annotation { "Feature Type Name" : "Feature", "Feature Type Description" : "" }
export const myFeature = defineFeature(function(context is Context, id is Id, definition is map)
    precondition{}
    {
        {
            var Q0;
            Q0=qCreatedBy(makeId("Top.planeOp"),FACE);
            var sketch = newSketch(context, id + "F0", { "sketchPlane" : qUnion([Q0])});
            skPoint(sketch, "E0.0", {"position": v(5.76, 3.36) * mm});
            skPoint(sketch, "E1.0", {"position": v(6.94, 3.46) * mm});
            skPoint(sketch, "E2.0", {"position": v(8.14, 3.52) * mm});
            skPoint(sketch, "E3.0", {"position": v(9.34, 3.55) * mm});
            skPoint(sketch, "E4.0", {"position": v(10.55, 3.56) * mm});
            skPoint(sketch, "E5.0", {"position": v(11.74, 3.54) * mm});
            skPoint(sketch, "E6.0", {"position": v(12.92, 3.51) * mm});
            skPoint(sketch, "E7.0", {"position": v(14.07, 3.48) * mm});
            skPoint(sketch, "E8.0", {"position": v(15.2, 3.46) * mm});
            skPoint(sketch, "E9.0", {"position": v(16.27, 3.44) * mm});
            skPoint(sketch, "E10.0", {"position": v(17.17, 3.43) * mm});
            skPoint(sketch, "E11.0", {"position": v(17.88, 3.43) * mm});
            skPoint(sketch, "E12.0", {"position": v(18.44, 3.43) * mm});
            skPoint(sketch, "E13.0", {"position": v(18.9, 3.43) * mm});
            skPoint(sketch, "E14.0", {"position": v(19.8, 3.43) * mm});
            skPoint(sketch, "E15.0", {"position": v(20.34, 3.43) * mm});
            skPoint(sketch, "E16.0", {"position": v(21, 3.42) * mm});
            skPoint(sketch, "E17.0", {"position": v(21.87, 3.4) * mm});
            skPoint(sketch, "E18.0", {"position": v(22.97, 3.37) * mm});
            skPoint(sketch, "E19.0", {"position": v(24.38, 3.33) * mm});
            skPoint(sketch, "E20.0", {"position": v(26.14, 3.27) * mm});
            skPoint(sketch, "E21.0", {"position": v(26.51, 3.2) * mm});
            skPoint(sketch, "E22.0", {"position": v(26.85, 3) * mm});
            skPoint(sketch, "E23.0", {"position": v(27.16, 2.72) * mm});
            skPoint(sketch, "E24.0", {"position": v(27.44, 2.35) * mm});
            skPoint(sketch, "E25.0", {"position": v(27.69, 1.92) * mm});
            skPoint(sketch, "E26.0", {"position": v(27.92, 1.45) * mm});
            skPoint(sketch, "E27.0", {"position": v(28.12, 0.94) * mm});
            skPoint(sketch, "E28.0", {"position": v(28.3, 0.43) * mm});
            skPoint(sketch, "E29.0", {"position": v(28.47, -0.07) * mm});
            skPoint(sketch, "E30.0", {"position": v(28.62, -0.55) * mm});
            skPoint(sketch, "E31.0", {"position": v(28.76, -1) * mm});
            skPoint(sketch, "E32.0", {"position": v(28.88, -1.37) * mm});
            skPoint(sketch, "E33.0", {"position": v(29.06, -1.72) * mm});
            skPoint(sketch, "E34.0", {"position": v(29.3, -2) * mm});
            skPoint(sketch, "E35.0", {"position": v(29.58, -2.16) * mm});
            skPoint(sketch, "E36.0", {"position": v(29.9, -2.22) * mm});
            skPoint(sketch, "E37.0", {"position": v(30.26, -2.13) * mm});
            skPoint(sketch, "E38.0", {"position": v(30.62, -1.89) * mm});
            skPoint(sketch, "E39.0", {"position": v(30.98, -1.47) * mm});
            skPoint(sketch, "E40.0", {"position": v(31.33, -0.85) * mm});
            skPoint(sketch, "E41.0", {"position": v(31.66, -0.02) * mm});
            skPoint(sketch, "E42.0", {"position": v(31.94, 1.04) * mm});
            skPoint(sketch, "E43.0", {"position": v(32.17, 2.36) * mm});
            skPoint(sketch, "E44.0", {"position": v(32.34, 3.95) * mm});
            skPoint(sketch, "E45.0", {"position": v(31.94, 5.71) * mm});
            skPoint(sketch, "E46.0", {"position": v(30.52, 7.1) * mm});
            skPoint(sketch, "E47.0", {"position": v(28.22, 8.13) * mm});
            skPoint(sketch, "E48.0", {"position": v(25.18, 8.86) * mm});
            skPoint(sketch, "E49.0", {"position": v(21.51, 9.33) * mm});
            skPoint(sketch, "E50.0", {"position": v(17.37, 9.58) * mm});
            skPoint(sketch, "E51.0", {"position": v(12.88, 9.65) * mm});
            skPoint(sketch, "E52.0", {"position": v(8.18, 9.59) * mm});
            skPoint(sketch, "E53.0", {"position": v(3.4, 9.42) * mm});
            skPoint(sketch, "E54.0", {"position": v(-14.33, 8.55) * mm});
            skPoint(sketch, "E55.0", {"position": v(-10.12, 8.78) * mm});
            skPoint(sketch, "E56.0", {"position": v(-5.9, 8.98) * mm});
            skPoint(sketch, "E57.0", {"position": v(-1.34, 9.2) * mm});
            skPoint(sketch, "E58.0", {"position": v(-19.1, 8.2) * mm});
            skPoint(sketch, "E59.0", {"position": v(-24.25, 7.73) * mm});
            skPoint(sketch, "E60.0", {"position": v(-29.6, 7.16) * mm});
            skPoint(sketch, "E61.0", {"position": v(-35, 6.5) * mm});
            skPoint(sketch, "E62.0", {"position": v(-40.24, 5.75) * mm});
            skPoint(sketch, "E63.0", {"position": v(-45.17, 4.92) * mm});
            skPoint(sketch, "E64.0", {"position": v(-49.6, 4.03) * mm});
            skPoint(sketch, "E65.0", {"position": v(-53.38, 3.07) * mm});
            skPoint(sketch, "E66.0", {"position": v(-56.31, 2.08) * mm});
            skPoint(sketch, "E67.0", {"position": v(-58.23, 1.04) * mm});
            skPoint(sketch, "E68.0", {"position": v(-58.96, -0.03) * mm});
            skPoint(sketch, "E69.0", {"position": v(-58.54, -1.04) * mm});
            skPoint(sketch, "E70.0", {"position": v(-57.22, -1.7) * mm});
            skPoint(sketch, "E71.0", {"position": v(-55.14, -2.02) * mm});
            skPoint(sketch, "E72.0", {"position": v(-49.2, -1.91) * mm});
            skPoint(sketch, "E73.0", {"position": v(-45.64, -1.57) * mm});
            skPoint(sketch, "E74.0", {"position": v(-41.85, -1.1) * mm});
            skPoint(sketch, "E75.0", {"position": v(-37.98, -0.57) * mm});
            skPoint(sketch, "E76.0", {"position": v(-34.17, 0) * mm});
            skPoint(sketch, "E77.0", {"position": v(-30.54, 0.55) * mm});
            skPoint(sketch, "E78.0", {"position": v(-27.24, 1.03) * mm});
            skPoint(sketch, "E79.0", {"position": v(-24.4, 1.4) * mm});
            skPoint(sketch, "E80.0", {"position": v(-20.27, 1.18) * mm});
            skPoint(sketch, "E81.0", {"position": v(-18.42, 0.62) * mm});
            skPoint(sketch, "E82.0", {"position": v(-16.71, -0.18) * mm});
            skPoint(sketch, "E83.0", {"position": v(-15.15, -1.14) * mm});
            skPoint(sketch, "E84.0", {"position": v(-22.27, 1.45) * mm});
            skPoint(sketch, "E85.0", {"position": v(-13.73, -2.24) * mm});
            skPoint(sketch, "E86.0", {"position": v(-12.46, -3.4) * mm});
            skPoint(sketch, "E87.0", {"position": v(-11.33, -4.59) * mm});
            skPoint(sketch, "E88.0", {"position": v(-10.34, -5.74) * mm});
            skPoint(sketch, "E89.0", {"position": v(-9.5, -6.8) * mm});
            skPoint(sketch, "E90.0", {"position": v(-8.8, -7.72) * mm});
            skPoint(sketch, "E91.0", {"position": v(-8.24, -8.44) * mm});
            skPoint(sketch, "E92.0", {"position": v(-8.78, -8.36) * mm});
            skPoint(sketch, "E93.0", {"position": v(-7.6, -9.13) * mm});
            skPoint(sketch, "E94.0", {"position": v(-6.87, -9.74) * mm});
            skPoint(sketch, "E95.0", {"position": v(-5.2, -10.7) * mm});
            skPoint(sketch, "E96.0", {"position": v(-6.06, -10.27) * mm});
            skPoint(sketch, "E97.0", {"position": v(-4.32, -11.02) * mm});
            skPoint(sketch, "E98.0", {"position": v(-3.44, -11.23) * mm});
            skPoint(sketch, "E99.0", {"position": v(-2.59, -11.32) * mm});
            skPoint(sketch, "E100.0", {"position": v(-1.8, -11.27) * mm});
            skPoint(sketch, "E101.0", {"position": v(-1.08, -11.09) * mm});
            skPoint(sketch, "E102.0", {"position": v(-0.47, -10.75) * mm});
            skPoint(sketch, "E103.0", {"position": v(0, -10.24) * mm});
            skPoint(sketch, "E104.0", {"position": v(0.31, -9.57) * mm});
            skPoint(sketch, "E105.0", {"position": v(0.6, -8.64) * mm});
            skPoint(sketch, "E106.0", {"position": v(0.9, -7.79) * mm});
            skPoint(sketch, "E107.0", {"position": v(1.18, -7) * mm});
            skPoint(sketch, "E108.0", {"position": v(1.44, -6.3) * mm});
            skPoint(sketch, "E109.0", {"position": v(1.67, -5.7) * mm});
            skPoint(sketch, "E110.0", {"position": v(1.84, -5.19) * mm});
            skPoint(sketch, "E111.0", {"position": v(1.95, -4.78) * mm});
            skPoint(sketch, "E112.0", {"position": v(1.98, -4.48) * mm});
            skPoint(sketch, "E113.0", {"position": v(1.92, -4.3) * mm});
            skPoint(sketch, "E114.0", {"position": v(1.48, -4.32) * mm});
            skPoint(sketch, "E115.0", {"position": v(1.08, -4.54) * mm});
            skPoint(sketch, "E116.0", {"position": v(0.17, -4.94) * mm});
            skPoint(sketch, "E117.0", {"position": v(-0.46, -4.93) * mm});
            skPoint(sketch, "E118.0", {"position": v(-0.84, -4.57) * mm});
            skPoint(sketch, "E119.0", {"position": v(-1, -3.93) * mm});
            skPoint(sketch, "E120.0", {"position": v(-0.98, -3.08) * mm});
            skPoint(sketch, "E121.0", {"position": v(-0.78, -2.1) * mm});
            skPoint(sketch, "E122.0", {"position": v(-0.45, -1.05) * mm});
            skPoint(sketch, "E123.0", {"position": v(0, 0) * mm});
            skPoint(sketch, "E124.0", {"position": v(0.54, 0.98) * mm});
            skPoint(sketch, "E125.0", {"position": v(1.13, 1.8) * mm});
            skPoint(sketch, "E126.0", {"position": v(1.76, 2.43) * mm});
            skPoint(sketch, "E127.0", {"position": v(2.4, 2.77) * mm});
            skPoint(sketch, "E128.0", {"position": v(3.48, 3.02) * mm});
            skPoint(sketch, "E129.0", {"position": v(4.6, 3.22) * mm});
            skLineSegment(sketch, "E130", {"start": v(-56.31, 2.08) * mm, "end": v(-53.38, 3.07) * mm});
            skLineSegment(sketch, "E131", {"start": v(-49.6, 4.03) * mm, "end": v(-53.38, 3.07) * mm});
            skLineSegment(sketch, "E132", {"start": v(-49.6, 4.03) * mm, "end": v(-45.17, 4.92) * mm});
            skLineSegment(sketch, "E133", {"start": v(-45.17, 4.92) * mm, "end": v(-40.24, 5.75) * mm});
            skLineSegment(sketch, "E134", {"start": v(-40.24, 5.75) * mm, "end": v(-35, 6.5) * mm});
            skLineSegment(sketch, "E135", {"start": v(-35, 6.5) * mm, "end": v(-29.6, 7.16) * mm});
            skLineSegment(sketch, "E136", {"start": v(-29.6, 7.16) * mm, "end": v(-24.25, 7.73) * mm});
            skLineSegment(sketch, "E137", {"start": v(-24.25, 7.73) * mm, "end": v(-19.1, 8.2) * mm});
            skLineSegment(sketch, "E138", {"start": v(-19.1, 8.2) * mm, "end": v(-14.33, 8.55) * mm});
            skLineSegment(sketch, "E139", {"start": v(-14.33, 8.55) * mm, "end": v(-10.12, 8.78) * mm});
            skLineSegment(sketch, "E140", {"start": v(-10.12, 8.78) * mm, "end": v(-5.9, 8.98) * mm});
            skLineSegment(sketch, "E141", {"start": v(-5.9, 8.98) * mm, "end": v(-1.34, 9.2) * mm});
            skLineSegment(sketch, "E142", {"start": v(-1.34, 9.2) * mm, "end": v(3.4, 9.42) * mm});
            skLineSegment(sketch, "E143", {"start": v(3.4, 9.42) * mm, "end": v(8.18, 9.59) * mm});
            skLineSegment(sketch, "E144", {"start": v(8.18, 9.59) * mm, "end": v(12.88, 9.65) * mm});
            skLineSegment(sketch, "E145", {"start": v(12.88, 9.65) * mm, "end": v(17.37, 9.58) * mm});
            skLineSegment(sketch, "E146", {"start": v(17.37, 9.58) * mm, "end": v(21.51, 9.33) * mm});
            skLineSegment(sketch, "E147", {"start": v(21.51, 9.33) * mm, "end": v(25.18, 8.86) * mm});
            skLineSegment(sketch, "E148", {"start": v(28.22, 8.13) * mm, "end": v(25.18, 8.86) * mm});
            skLineSegment(sketch, "E149", {"start": v(28.22, 8.13) * mm, "end": v(30.52, 7.1) * mm});
            skLineSegment(sketch, "E150", {"start": v(30.52, 7.1) * mm, "end": v(31.94, 5.71) * mm});
            skLineSegment(sketch, "E151", {"start": v(31.94, 5.71) * mm, "end": v(32.34, 3.95) * mm});
            skLineSegment(sketch, "E152", {"start": v(32.34, 3.95) * mm, "end": v(32.17, 2.36) * mm});
            skLineSegment(sketch, "E153", {"start": v(32.17, 2.36) * mm, "end": v(31.94, 1.04) * mm});
            skLineSegment(sketch, "E154", {"start": v(31.94, 1.04) * mm, "end": v(31.66, -0.02) * mm});
            skLineSegment(sketch, "E155", {"start": v(31.66, -0.02) * mm, "end": v(31.33, -0.85) * mm});
            skLineSegment(sketch, "E156", {"start": v(31.33, -0.85) * mm, "end": v(30.98, -1.47) * mm});
            skLineSegment(sketch, "E157", {"start": v(30.98, -1.47) * mm, "end": v(30.62, -1.89) * mm});
            skLineSegment(sketch, "E158", {"start": v(30.62, -1.89) * mm, "end": v(30.26, -2.13) * mm});
            skLineSegment(sketch, "E159", {"start": v(30.26, -2.13) * mm, "end": v(29.9, -2.22) * mm});
            skLineSegment(sketch, "E160", {"start": v(29.9, -2.22) * mm, "end": v(29.58, -2.16) * mm});
            skLineSegment(sketch, "E161", {"start": v(29.58, -2.16) * mm, "end": v(29.3, -2) * mm});
            skLineSegment(sketch, "E162", {"start": v(29.3, -2) * mm, "end": v(29.06, -1.72) * mm});
            skLineSegment(sketch, "E163", {"start": v(29.06, -1.72) * mm, "end": v(28.88, -1.37) * mm});
            skLineSegment(sketch, "E164", {"start": v(28.88, -1.37) * mm, "end": v(28.76, -1) * mm});
            skLineSegment(sketch, "E165", {"start": v(28.76, -1) * mm, "end": v(28.62, -0.55) * mm});
            skLineSegment(sketch, "E166", {"start": v(28.62, -0.55) * mm, "end": v(28.47, -0.07) * mm});
            skLineSegment(sketch, "E167", {"start": v(28.47, -0.07) * mm, "end": v(28.3, 0.43) * mm});
            skLineSegment(sketch, "E168", {"start": v(28.3, 0.43) * mm, "end": v(28.12, 0.94) * mm});
            skLineSegment(sketch, "E169", {"start": v(28.12, 0.94) * mm, "end": v(27.92, 1.45) * mm});
            skLineSegment(sketch, "E170", {"start": v(27.92, 1.45) * mm, "end": v(27.69, 1.92) * mm});
            skLineSegment(sketch, "E171", {"start": v(27.69, 1.92) * mm, "end": v(27.44, 2.35) * mm});
            skLineSegment(sketch, "E172", {"start": v(27.16, 2.72) * mm, "end": v(27.44, 2.35) * mm});
            skLineSegment(sketch, "E173", {"start": v(26.85, 3) * mm, "end": v(27.16, 2.72) * mm});
            skLineSegment(sketch, "E174", {"start": v(26.51, 3.2) * mm, "end": v(26.85, 3) * mm});
            skLineSegment(sketch, "E175", {"start": v(26.14, 3.27) * mm, "end": v(26.51, 3.2) * mm});
            skLineSegment(sketch, "E176", {"start": v(24.38, 3.33) * mm, "end": v(26.14, 3.27) * mm});
            skLineSegment(sketch, "E177", {"start": v(22.97, 3.37) * mm, "end": v(24.38, 3.33) * mm});
            skLineSegment(sketch, "E178", {"start": v(21.87, 3.4) * mm, "end": v(22.97, 3.37) * mm});
            skLineSegment(sketch, "E179", {"start": v(21, 3.42) * mm, "end": v(21.87, 3.4) * mm});
            skLineSegment(sketch, "E180", {"start": v(20.34, 3.43) * mm, "end": v(21, 3.42) * mm});
            skLineSegment(sketch, "E181", {"start": v(19.8, 3.43) * mm, "end": v(20.34, 3.43) * mm});
            skLineSegment(sketch, "E182", {"start": v(18.9, 3.43) * mm, "end": v(19.8, 3.43) * mm});
            skLineSegment(sketch, "E183", {"start": v(18.44, 3.43) * mm, "end": v(18.9, 3.43) * mm});
            skLineSegment(sketch, "E184", {"start": v(18.44, 3.43) * mm, "end": v(17.88, 3.43) * mm});
            skLineSegment(sketch, "E185", {"start": v(17.88, 3.43) * mm, "end": v(17.17, 3.43) * mm});
            skLineSegment(sketch, "E186", {"start": v(17.17, 3.43) * mm, "end": v(16.27, 3.44) * mm});
            skLineSegment(sketch, "E187", {"start": v(16.27, 3.44) * mm, "end": v(15.2, 3.46) * mm});
            skLineSegment(sketch, "E188", {"start": v(15.2, 3.46) * mm, "end": v(14.07, 3.48) * mm});
            skLineSegment(sketch, "E189", {"start": v(14.07, 3.48) * mm, "end": v(12.92, 3.51) * mm});
            skLineSegment(sketch, "E190", {"start": v(-1, -3.93) * mm, "end": v(-0.84, -4.57) * mm});
            skLineSegment(sketch, "E191", {"start": v(-0.84, -4.57) * mm, "end": v(-0.46, -4.93) * mm});
            skLineSegment(sketch, "E192", {"start": v(-0.46, -4.93) * mm, "end": v(0.17, -4.94) * mm});
            skLineSegment(sketch, "E193", {"start": v(0.17, -4.94) * mm, "end": v(1.08, -4.54) * mm});
            skLineSegment(sketch, "E194", {"start": v(1.08, -4.54) * mm, "end": v(1.48, -4.32) * mm});
            skLineSegment(sketch, "E195", {"start": v(1.48, -4.32) * mm, "end": v(1.92, -4.3) * mm});
            skLineSegment(sketch, "E196", {"start": v(1.92, -4.3) * mm, "end": v(1.98, -4.48) * mm});
            skLineSegment(sketch, "E197", {"start": v(1.98, -4.48) * mm, "end": v(1.95, -4.78) * mm});
            skLineSegment(sketch, "E198", {"start": v(1.95, -4.78) * mm, "end": v(1.84, -5.19) * mm});
            skLineSegment(sketch, "E199", {"start": v(1.84, -5.19) * mm, "end": v(1.67, -5.7) * mm});
            skLineSegment(sketch, "E200", {"start": v(1.67, -5.7) * mm, "end": v(1.44, -6.3) * mm});
            skLineSegment(sketch, "E201", {"start": v(1.44, -6.3) * mm, "end": v(1.18, -7) * mm});
            skLineSegment(sketch, "E202", {"start": v(1.18, -7) * mm, "end": v(0.9, -7.79) * mm});
            skLineSegment(sketch, "E203", {"start": v(-1, -3.93) * mm, "end": v(-0.98, -3.08) * mm});
            skLineSegment(sketch, "E204", {"start": v(-0.98, -3.08) * mm, "end": v(-0.78, -2.1) * mm});
            skLineSegment(sketch, "E205", {"start": v(-56.31, 2.08) * mm, "end": v(-58.23, 1.04) * mm});
            skLineSegment(sketch, "E206", {"start": v(-58.23, 1.04) * mm, "end": v(-58.96, -0.03) * mm});
            skLineSegment(sketch, "E207", {"start": v(-58.96, -0.03) * mm, "end": v(-58.54, -1.04) * mm});
            skLineSegment(sketch, "E208", {"start": v(-58.54, -1.04) * mm, "end": v(-57.22, -1.7) * mm});
            skLineSegment(sketch, "E209", {"start": v(-57.22, -1.7) * mm, "end": v(-55.14, -2.02) * mm});
            skLineSegment(sketch, "E210", {"start": v(-55.14, -2.02) * mm, "end": v(-49.2, -1.91) * mm});
            skLineSegment(sketch, "E211", {"start": v(-0.78, -2.1) * mm, "end": v(-0.45, -1.05) * mm});
            skLineSegment(sketch, "E212", {"start": v(0, 0) * mm, "end": v(-0.45, -1.05) * mm});
            skLineSegment(sketch, "E213", {"start": v(0, 0) * mm, "end": v(0.54, 0.98) * mm});
            skLineSegment(sketch, "E214", {"start": v(0.54, 0.98) * mm, "end": v(1.13, 1.8) * mm});
            skLineSegment(sketch, "E215", {"start": v(1.13, 1.8) * mm, "end": v(1.76, 2.43) * mm});
            skLineSegment(sketch, "E216", {"start": v(1.76, 2.43) * mm, "end": v(2.4, 2.77) * mm});
            skLineSegment(sketch, "E217", {"start": v(2.4, 2.77) * mm, "end": v(3.48, 3.02) * mm});
            skLineSegment(sketch, "E218", {"start": v(3.48, 3.02) * mm, "end": v(4.6, 3.22) * mm});
            skLineSegment(sketch, "E219", {"start": v(4.6, 3.22) * mm, "end": v(5.76, 3.36) * mm});
            skLineSegment(sketch, "E220", {"start": v(5.76, 3.36) * mm, "end": v(6.94, 3.46) * mm});
            skLineSegment(sketch, "E221", {"start": v(6.94, 3.46) * mm, "end": v(8.14, 3.52) * mm});
            skLineSegment(sketch, "E222", {"start": v(8.14, 3.52) * mm, "end": v(9.34, 3.55) * mm});
            skLineSegment(sketch, "E223", {"start": v(9.34, 3.55) * mm, "end": v(10.55, 3.56) * mm});
            skLineSegment(sketch, "E224", {"start": v(10.55, 3.56) * mm, "end": v(11.74, 3.54) * mm});
            skLineSegment(sketch, "E225", {"start": v(11.74, 3.54) * mm, "end": v(12.92, 3.51) * mm});
            skLineSegment(sketch, "E226", {"start": v(0.9, -7.79) * mm, "end": v(0.6, -8.64) * mm});
            skLineSegment(sketch, "E227", {"start": v(0.6, -8.64) * mm, "end": v(0.31, -9.57) * mm});
            skLineSegment(sketch, "E228", {"start": v(0.31, -9.57) * mm, "end": v(0, -10.24) * mm});
            skLineSegment(sketch, "E229", {"start": v(0, -10.24) * mm, "end": v(-0.47, -10.75) * mm});
            skLineSegment(sketch, "E230", {"start": v(-0.47, -10.75) * mm, "end": v(-1.08, -11.09) * mm});
            skLineSegment(sketch, "E231", {"start": v(-1.08, -11.09) * mm, "end": v(-1.8, -11.27) * mm});
            skLineSegment(sketch, "E232", {"start": v(-1.8, -11.27) * mm, "end": v(-2.59, -11.32) * mm});
            skLineSegment(sketch, "E233", {"start": v(-2.59, -11.32) * mm, "end": v(-3.44, -11.23) * mm});
            skLineSegment(sketch, "E234", {"start": v(-4.32, -11.02) * mm, "end": v(-3.44, -11.23) * mm});
            skLineSegment(sketch, "E235", {"start": v(-5.2, -10.7) * mm, "end": v(-4.32, -11.02) * mm});
            skLineSegment(sketch, "E236", {"start": v(-6.06, -10.27) * mm, "end": v(-5.2, -10.7) * mm});
            skLineSegment(sketch, "E237", {"start": v(-6.87, -9.74) * mm, "end": v(-6.06, -10.27) * mm});
            skLineSegment(sketch, "E238", {"start": v(-7.6, -9.13) * mm, "end": v(-6.87, -9.74) * mm});
            skLineSegment(sketch, "E239", {"start": v(-8.24, -8.44) * mm, "end": v(-7.6, -9.13) * mm});
            skLineSegment(sketch, "E240", {"start": v(-8.8, -7.72) * mm, "end": v(-8.24, -8.44) * mm});
            skLineSegment(sketch, "E241", {"start": v(-9.5, -6.8) * mm, "end": v(-8.8, -7.72) * mm});
            skLineSegment(sketch, "E242", {"start": v(-10.34, -5.74) * mm, "end": v(-9.5, -6.8) * mm});
            skLineSegment(sketch, "E243", {"start": v(-11.33, -4.59) * mm, "end": v(-10.34, -5.74) * mm});
            skLineSegment(sketch, "E244", {"start": v(-12.46, -3.4) * mm, "end": v(-11.33, -4.59) * mm});
            skLineSegment(sketch, "E245", {"start": v(-13.73, -2.24) * mm, "end": v(-12.46, -3.4) * mm});
            skLineSegment(sketch, "E246", {"start": v(-15.15, -1.14) * mm, "end": v(-13.73, -2.24) * mm});
            skLineSegment(sketch, "E247", {"start": v(-16.71, -0.18) * mm, "end": v(-15.15, -1.14) * mm});
            skLineSegment(sketch, "E248", {"start": v(-18.42, 0.62) * mm, "end": v(-16.71, -0.18) * mm});
            skLineSegment(sketch, "E249", {"start": v(-20.27, 1.18) * mm, "end": v(-18.42, 0.62) * mm});
            skLineSegment(sketch, "E250", {"start": v(-22.27, 1.45) * mm, "end": v(-20.27, 1.18) * mm});
            skLineSegment(sketch, "E251", {"start": v(-24.4, 1.4) * mm, "end": v(-22.27, 1.45) * mm});
            skLineSegment(sketch, "E252", {"start": v(-27.24, 1.03) * mm, "end": v(-24.4, 1.4) * mm});
            skLineSegment(sketch, "E253", {"start": v(-30.54, 0.55) * mm, "end": v(-27.24, 1.03) * mm});
            skLineSegment(sketch, "E254", {"start": v(-34.17, 0) * mm, "end": v(-30.54, 0.55) * mm});
            skLineSegment(sketch, "E255", {"start": v(-37.98, -0.57) * mm, "end": v(-34.17, 0) * mm});
            skLineSegment(sketch, "E256", {"start": v(-41.85, -1.1) * mm, "end": v(-37.98, -0.57) * mm});
            skLineSegment(sketch, "E257", {"start": v(-45.64, -1.57) * mm, "end": v(-41.85, -1.1) * mm});
            skLineSegment(sketch, "E258", {"start": v(-49.2, -1.91) * mm, "end": v(-45.64, -1.57) * mm});
            skLineSegment(sketch, "E259", {"start": v(39.91, 21.1) * mm, "end": v(-64.45, 21.1) * mm});
            skSolve(sketch);
        }
        {
            var Q0;
            Q0=makeQuery(id+"F0.imprint","IMPRINT",FACE,{"disambiguationData":[TD([[makeQuery(id+"F0.imprint","IMPRINT",EDGE,{"derivedFrom":sQuery(id+"F0.wireOp",EDGE,"E130")}),-1.0]])]});
            extrude(context, id + "F1", {"entities" : qUnion([Q0]), "endBound" : BoundingType.SYMMETRIC, "depth" : 10 * mm});
        }
        {
            var Q0;
            Q0=makeQuery(id+"F1.opExtrude","SWEPT_BODY",BODY,{"disambiguationData":[OSD([sQuery(id+"F0.wireOp",EDGE,"E130"),sQuery(id+"F0.wireOp",EDGE,"E131"),sQuery(id+"F0.wireOp",EDGE,"E132"),sQuery(id+"F0.wireOp",EDGE,"E133"),sQuery(id+"F0.wireOp",EDGE,"E134"),sQuery(id+"F0.wireOp",EDGE,"E135"),sQuery(id+"F0.wireOp",EDGE,"E136"),sQuery(id+"F0.wireOp",EDGE,"E137"),sQuery(id+"F0.wireOp",EDGE,"E138"),sQuery(id+"F0.wireOp",EDGE,"E139"),sQuery(id+"F0.wireOp",EDGE,"E140"),sQuery(id+"F0.wireOp",EDGE,"E141"),sQuery(id+"F0.wireOp",EDGE,"E142"),sQuery(id+"F0.wireOp",EDGE,"E143"),sQuery(id+"F0.wireOp",EDGE,"E144"),sQuery(id+"F0.wireOp",EDGE,"E145"),sQuery(id+"F0.wireOp",EDGE,"E146"),sQuery(id+"F0.wireOp",EDGE,"E147"),sQuery(id+"F0.wireOp",EDGE,"E148"),sQuery(id+"F0.wireOp",EDGE,"E149"),sQuery(id+"F0.wireOp",EDGE,"E150"),sQuery(id+"F0.wireOp",EDGE,"E151"),sQuery(id+"F0.wireOp",EDGE,"E152"),sQuery(id+"F0.wireOp",EDGE,"E153"),sQuery(id+"F0.wireOp",EDGE,"E154"),sQuery(id+"F0.wireOp",EDGE,"E155"),sQuery(id+"F0.wireOp",EDGE,"E156"),sQuery(id+"F0.wireOp",EDGE,"E157"),sQuery(id+"F0.wireOp",EDGE,"E158"),sQuery(id+"F0.wireOp",EDGE,"E159"),sQuery(id+"F0.wireOp",EDGE,"E160"),sQuery(id+"F0.wireOp",EDGE,"E161"),sQuery(id+"F0.wireOp",EDGE,"E162"),sQuery(id+"F0.wireOp",EDGE,"E163"),sQuery(id+"F0.wireOp",EDGE,"E164"),sQuery(id+"F0.wireOp",EDGE,"E165"),sQuery(id+"F0.wireOp",EDGE,"E166"),sQuery(id+"F0.wireOp",EDGE,"E167"),sQuery(id+"F0.wireOp",EDGE,"E168"),sQuery(id+"F0.wireOp",EDGE,"E169"),sQuery(id+"F0.wireOp",EDGE,"E170"),sQuery(id+"F0.wireOp",EDGE,"E171"),sQuery(id+"F0.wireOp",EDGE,"E172"),sQuery(id+"F0.wireOp",EDGE,"E173"),sQuery(id+"F0.wireOp",EDGE,"E174"),sQuery(id+"F0.wireOp",EDGE,"E175"),sQuery(id+"F0.wireOp",EDGE,"E176"),sQuery(id+"F0.wireOp",EDGE,"E177"),sQuery(id+"F0.wireOp",EDGE,"E178"),sQuery(id+"F0.wireOp",EDGE,"E179"),sQuery(id+"F0.wireOp",EDGE,"E180"),sQuery(id+"F0.wireOp",EDGE,"E181"),sQuery(id+"F0.wireOp",EDGE,"E182"),sQuery(id+"F0.wireOp",EDGE,"E183"),sQuery(id+"F0.wireOp",EDGE,"E184"),sQuery(id+"F0.wireOp",EDGE,"E185"),sQuery(id+"F0.wireOp",EDGE,"E186"),sQuery(id+"F0.wireOp",EDGE,"E187"),sQuery(id+"F0.wireOp",EDGE,"E188"),sQuery(id+"F0.wireOp",EDGE,"E189"),sQuery(id+"F0.wireOp",EDGE,"E190"),sQuery(id+"F0.wireOp",EDGE,"E191"),sQuery(id+"F0.wireOp",EDGE,"E192"),sQuery(id+"F0.wireOp",EDGE,"E193"),sQuery(id+"F0.wireOp",EDGE,"E194"),sQuery(id+"F0.wireOp",EDGE,"E195"),sQuery(id+"F0.wireOp",EDGE,"E196"),sQuery(id+"F0.wireOp",EDGE,"E197"),sQuery(id+"F0.wireOp",EDGE,"E198"),sQuery(id+"F0.wireOp",EDGE,"E199"),sQuery(id+"F0.wireOp",EDGE,"E200"),sQuery(id+"F0.wireOp",EDGE,"E201"),sQuery(id+"F0.wireOp",EDGE,"E202"),sQuery(id+"F0.wireOp",EDGE,"E203"),sQuery(id+"F0.wireOp",EDGE,"E204"),sQuery(id+"F0.wireOp",EDGE,"E205"),sQuery(id+"F0.wireOp",EDGE,"E206"),sQuery(id+"F0.wireOp",EDGE,"E207"),sQuery(id+"F0.wireOp",EDGE,"E208"),sQuery(id+"F0.wireOp",EDGE,"E209"),sQuery(id+"F0.wireOp",EDGE,"E210"),sQuery(id+"F0.wireOp",EDGE,"E211"),sQuery(id+"F0.wireOp",EDGE,"E212"),sQuery(id+"F0.wireOp",EDGE,"E213"),sQuery(id+"F0.wireOp",EDGE,"E214"),sQuery(id+"F0.wireOp",EDGE,"E215"),sQuery(id+"F0.wireOp",EDGE,"E216"),sQuery(id+"F0.wireOp",EDGE,"E217"),sQuery(id+"F0.wireOp",EDGE,"E218"),sQuery(id+"F0.wireOp",EDGE,"E219"),sQuery(id+"F0.wireOp",EDGE,"E220"),sQuery(id+"F0.wireOp",EDGE,"E221"),sQuery(id+"F0.wireOp",EDGE,"E222"),sQuery(id+"F0.wireOp",EDGE,"E223"),sQuery(id+"F0.wireOp",EDGE,"E224"),sQuery(id+"F0.wireOp",EDGE,"E225"),sQuery(id+"F0.wireOp",EDGE,"E226"),sQuery(id+"F0.wireOp",EDGE,"E227"),sQuery(id+"F0.wireOp",EDGE,"E228"),sQuery(id+"F0.wireOp",EDGE,"E229"),sQuery(id+"F0.wireOp",EDGE,"E230"),sQuery(id+"F0.wireOp",EDGE,"E231"),sQuery(id+"F0.wireOp",EDGE,"E232"),sQuery(id+"F0.wireOp",EDGE,"E233"),sQuery(id+"F0.wireOp",EDGE,"E234"),sQuery(id+"F0.wireOp",EDGE,"E235"),sQuery(id+"F0.wireOp",EDGE,"E236"),sQuery(id+"F0.wireOp",EDGE,"E237"),sQuery(id+"F0.wireOp",EDGE,"E238"),sQuery(id+"F0.wireOp",EDGE,"E239"),sQuery(id+"F0.wireOp",EDGE,"E240"),sQuery(id+"F0.wireOp",EDGE,"E241"),sQuery(id+"F0.wireOp",EDGE,"E242"),sQuery(id+"F0.wireOp",EDGE,"E243"),sQuery(id+"F0.wireOp",EDGE,"E244"),sQuery(id+"F0.wireOp",EDGE,"E245"),sQuery(id+"F0.wireOp",EDGE,"E246"),sQuery(id+"F0.wireOp",EDGE,"E247"),sQuery(id+"F0.wireOp",EDGE,"E248"),sQuery(id+"F0.wireOp",EDGE,"E249"),sQuery(id+"F0.wireOp",EDGE,"E250"),sQuery(id+"F0.wireOp",EDGE,"E251"),sQuery(id+"F0.wireOp",EDGE,"E252"),sQuery(id+"F0.wireOp",EDGE,"E253"),sQuery(id+"F0.wireOp",EDGE,"E254"),sQuery(id+"F0.wireOp",EDGE,"E255"),sQuery(id+"F0.wireOp",EDGE,"E256"),sQuery(id+"F0.wireOp",EDGE,"E257"),sQuery(id+"F0.wireOp",EDGE,"E258")])]});
            var Q1;
            Q1=sQuery(id+"F0.wireOp",EDGE,"E259");
            transform(context, id + "F2", {"entities" : qUnion([Q0]), "transformType" : TransformType.ROTATION, "transformAxis" : qUnion([Q1]), "angle" : 180 * degree, "makeCopy" : false});
        }
        {
            var Q0;
            Q0=qCreatedBy(makeId("Front.planeOp"),FACE);
            cPlane(context, id + "F3", {"entities" : qUnion([Q0]), "cplaneType" : CPlaneType.OFFSET, "offset" : 32 * mm, "oppositeDirection" : true, "width" : 150 * mm, "height" : 150 * mm});
        }
        {
            var Q0;
            Q0=qCreatedBy(id+"F3.planeOp",FACE);
            var sketch = newSketch(context, id + "F4", { "sketchPlane" : qUnion([Q0])});
            skPoint(sketch, "E260.0", {"position": v(25.18, 5) * mm});
            skPoint(sketch, "E261.0", {"position": v(25.18, -5) * mm});
            skPoint(sketch, "E262.0", {"position": v(-45.17, -5) * mm});
            skPoint(sketch, "E263.0", {"position": v(-45.17, 5) * mm});
            skPoint(sketch, "E264.0", {"position": v(-58.23, 5) * mm});
            skPoint(sketch, "E265.0", {"position": v(-58.23, -5) * mm});
            skLineSegment(sketch, "E266.bottom", {"start": v(-58.23, 5) * mm, "end": v(-45.17, 5) * mm});
            skLineSegment(sketch, "E266.top", {"start": v(-58.23, -5) * mm, "end": v(-45.17, -5) * mm});
            skLineSegment(sketch, "E266.left", {"start": v(-58.23, 5) * mm, "end": v(-58.23, -5) * mm});
            skLineSegment(sketch, "E266.right", {"start": v(-45.17, 5) * mm, "end": v(-45.17, -5) * mm});
            skCircle(sketch, "E267", {"center": v(-48.96, 0) * mm, "radius": 3 * mm});
            skPoint(sketch, "E267.centerSnap0", {"position": v(-45.17, 0) * mm});
            skLineSegment(sketch, "E268.bottom", {"start": v(-45.17, 5) * mm, "end": v(25.18, 5) * mm});
            skLineSegment(sketch, "E268.top", {"start": v(-45.17, -5) * mm, "end": v(25.18, -5) * mm});
            skLineSegment(sketch, "E268.right", {"start": v(25.18, 5) * mm, "end": v(25.18, -5) * mm});
            skLineSegment(sketch, "E269.0", {"start": v(-40.24, -5) * mm, "end": v(-40.24, 5) * mm});
            skText(sketch, "E270", { "text": "Les Furieux", "fontName": "OpenSans-Bold.ttf"});
            skPoint(sketch, "E271", {"position": v(-10, 0) * mm});
            skPoint(sketch, "E272", {"position": v(-10, -5) * mm});
            skPoint(sketch, "E273.positionSnap0", {"position": v(-40.24, 0) * mm});
            const initialGuessF4  = {"E270": [-0.04202, -0.004, 1, 0, 0.008]};
            skSetInitialGuess(sketch, initialGuessF4);
            skSolve(sketch);
        }
        {
            var Q0;
            Q0=makeQuery(id+"F4.imprint","IMPRINT",FACE,{"disambiguationData":[TD([[makeQuery(id+"F4.imprint","IMPRINT",EDGE,{"derivedFrom":sQuery(id+"F4.wireOp",EDGE,"E267")}),1.0]])]});
            extrude(context, id + "F5", {"entities" : qUnion([Q0]), "operationType" : NewBodyOperationType.REMOVE, "endBound" : BoundingType.THROUGH_ALL, "oppositeDirection" : true, "depth" : 25 * mm});
        }
        {
            var Q0;
            Q0=makeQuery(id+"F4.imprint","IMPRINT",FACE,{"disambiguationData":[TD([[makeQuery(id+"F4.imprint","IMPRINT",EDGE,{"derivedFrom":sQuery(id+"F4.wireOp",EDGE,"E270.sketch_text.stroke-52")}),-1.0]])]});
            var Q1;
            Q1=makeQuery(id+"F4.imprint","IMPRINT",FACE,{"disambiguationData":[TD([[makeQuery(id+"F4.imprint","IMPRINT",EDGE,{"derivedFrom":sQuery(id+"F4.wireOp",EDGE,"E270.sketch_text.stroke-62")}),-1.0]])]});
            var Q2;
            Q2=makeQuery(id+"F4.imprint","IMPRINT",FACE,{"disambiguationData":[TD([[makeQuery(id+"F4.imprint","IMPRINT",EDGE,{"derivedFrom":sQuery(id+"F4.wireOp",EDGE,"E270.sketch_text.stroke-79")}),-1.0]])]});
            var Q3;
            Q3=makeQuery(id+"F4.imprint","IMPRINT",FACE,{"disambiguationData":[TD([[makeQuery(id+"F4.imprint","IMPRINT",EDGE,{"derivedFrom":sQuery(id+"F4.wireOp",EDGE,"E270.sketch_text.stroke-97")}),-1.0]])]});
            var Q4;
            Q4=makeQuery(id+"F4.imprint","IMPRINT",FACE,{"disambiguationData":[TD([[makeQuery(id+"F4.imprint","IMPRINT",EDGE,{"derivedFrom":sQuery(id+"F4.wireOp",EDGE,"E270.sketch_text.stroke-92")}),-1.0]])]});
            var Q5;
            Q5=makeQuery(id+"F4.imprint","IMPRINT",FACE,{"disambiguationData":[TD([[makeQuery(id+"F4.imprint","IMPRINT",EDGE,{"derivedFrom":sQuery(id+"F4.wireOp",EDGE,"E270.sketch_text.stroke-101")}),-1.0]])]});
            var Q6;
            Q6=makeQuery(id+"F4.imprint","IMPRINT",FACE,{"disambiguationData":[TD([[makeQuery(id+"F4.imprint","IMPRINT",EDGE,{"derivedFrom":sQuery(id+"F4.wireOp",EDGE,"E270.sketch_text.stroke-121")}),-1.0]])]});
            var Q7;
            Q7=makeQuery(id+"F4.imprint","IMPRINT",FACE,{"disambiguationData":[TD([[makeQuery(id+"F4.imprint","IMPRINT",EDGE,{"derivedFrom":sQuery(id+"F4.wireOp",EDGE,"E270.sketch_text.stroke-138")}),-1.0]])]});
            extrude(context, id + "F6", {"entities" : qUnion([Q0, Q1, Q2, Q3, Q4, Q5, Q6, Q7]), "operationType" : NewBodyOperationType.REMOVE, "oppositeDirection" : true, "depth" : 4 * mm});
        }
        {
            var Q0;
            {var subQ0=sQuery(id+"F4.wireOp",EDGE,"E270.sketch_text.stroke-2");Q0=makeQuery(id+"F4.imprint","IMPRINT",FACE,{"disambiguationData":[TD([[makeQuery(id+"F4.imprint","IMPRINT",EDGE,{"derivedFrom":subQ0}),-1.0]])]});}
            var Q1;
            {var subQ5=sQuery(id+"F4.wireOp",EDGE,"E270.sketch_text.stroke-0");Q1=makeQuery(id+"F4.imprint","IMPRINT",FACE,{"disambiguationData":[TD([[makeQuery(id+"F4.imprint","IMPRINT",EDGE,{"derivedFrom":subQ5}),-1.0]])]});}
            var Q2;
            Q2=makeQuery(id+"F4.imprint","IMPRINT",FACE,{"disambiguationData":[TD([[makeQuery(id+"F4.imprint","IMPRINT",EDGE,{"derivedFrom":sQuery(id+"F4.wireOp",EDGE,"E270.sketch_text.stroke-6")}),-1.0]])]});
            var Q3;
            Q3=makeQuery(id+"F4.imprint","IMPRINT",FACE,{"disambiguationData":[TD([[makeQuery(id+"F4.imprint","IMPRINT",EDGE,{"derivedFrom":sQuery(id+"F4.wireOp",EDGE,"E270.sketch_text.stroke-26")}),-1.0]])]});
            extrude(context, id + "F7", {"entities" : qUnion([Q0, Q1, Q2, Q3]), "operationType" : NewBodyOperationType.REMOVE, "oppositeDirection" : true, "depth" : 7 * mm});
        }
        {
            var Q0;
            Q0=qCreatedBy(makeId("Top.planeOp"),FACE);
            var sketch = newSketch(context, id + "F8", { "sketchPlane" : qUnion([Q0])});
            skPoint(sketch, "E274.0", {"position": v(5.76, 3.36) * mm});
            skPoint(sketch, "E275.0", {"position": v(6.94, 3.46) * mm});
            skPoint(sketch, "E276.0", {"position": v(8.14, 3.52) * mm});
            skPoint(sketch, "E277.0", {"position": v(9.34, 3.55) * mm});
            skPoint(sketch, "E278.0", {"position": v(10.55, 3.56) * mm});
            skPoint(sketch, "E279.0", {"position": v(11.74, 3.54) * mm});
            skPoint(sketch, "E280.0", {"position": v(12.92, 3.51) * mm});
            skPoint(sketch, "E281.0", {"position": v(14.07, 3.48) * mm});
            skPoint(sketch, "E282.0", {"position": v(15.2, 3.46) * mm});
            skPoint(sketch, "E283.0", {"position": v(16.27, 3.44) * mm});
            skPoint(sketch, "E284.0", {"position": v(17.17, 3.43) * mm});
            skPoint(sketch, "E285.0", {"position": v(17.88, 3.43) * mm});
            skPoint(sketch, "E286.0", {"position": v(18.44, 3.43) * mm});
            skPoint(sketch, "E287.0", {"position": v(18.9, 3.43) * mm});
            skPoint(sketch, "E288.0", {"position": v(19.8, 3.43) * mm});
            skPoint(sketch, "E289.0", {"position": v(20.34, 3.43) * mm});
            skPoint(sketch, "E290.0", {"position": v(21, 3.42) * mm});
            skPoint(sketch, "E291.0", {"position": v(21.87, 3.4) * mm});
            skPoint(sketch, "E292.0", {"position": v(22.97, 3.37) * mm});
            skPoint(sketch, "E293.0", {"position": v(24.38, 3.33) * mm});
            skPoint(sketch, "E294.0", {"position": v(26.14, 3.27) * mm});
            skPoint(sketch, "E295.0", {"position": v(26.51, 3.2) * mm});
            skPoint(sketch, "E296.0", {"position": v(26.85, 3) * mm});
            skPoint(sketch, "E297.0", {"position": v(27.16, 2.72) * mm});
            skPoint(sketch, "E298.0", {"position": v(27.44, 2.35) * mm});
            skPoint(sketch, "E299.0", {"position": v(27.69, 1.92) * mm});
            skPoint(sketch, "E300.0", {"position": v(27.92, 1.45) * mm});
            skPoint(sketch, "E301.0", {"position": v(28.12, 0.94) * mm});
            skPoint(sketch, "E302.0", {"position": v(28.3, 0.43) * mm});
            skPoint(sketch, "E303.0", {"position": v(28.47, -0.07) * mm});
            skPoint(sketch, "E304.0", {"position": v(28.62, -0.55) * mm});
            skPoint(sketch, "E305.0", {"position": v(28.76, -1) * mm});
            skPoint(sketch, "E306.0", {"position": v(28.88, -1.37) * mm});
            skPoint(sketch, "E307.0", {"position": v(29.06, -1.72) * mm});
            skPoint(sketch, "E308.0", {"position": v(29.3, -2) * mm});
            skPoint(sketch, "E309.0", {"position": v(29.58, -2.16) * mm});
            skPoint(sketch, "E310.0", {"position": v(29.9, -2.22) * mm});
            skPoint(sketch, "E311.0", {"position": v(30.26, -2.13) * mm});
            skPoint(sketch, "E312.0", {"position": v(30.62, -1.89) * mm});
            skPoint(sketch, "E313.0", {"position": v(30.98, -1.47) * mm});
            skPoint(sketch, "E314.0", {"position": v(31.33, -0.85) * mm});
            skPoint(sketch, "E315.0", {"position": v(31.66, -0.02) * mm});
            skPoint(sketch, "E316.0", {"position": v(31.94, 1.04) * mm});
            skPoint(sketch, "E317.0", {"position": v(32.17, 2.36) * mm});
            skPoint(sketch, "E318.0", {"position": v(32.34, 3.95) * mm});
            skPoint(sketch, "E319.0", {"position": v(31.94, 5.71) * mm});
            skPoint(sketch, "E320.0", {"position": v(30.52, 7.1) * mm});
            skPoint(sketch, "E321.0", {"position": v(28.22, 8.13) * mm});
            skPoint(sketch, "E322.0", {"position": v(25.18, 8.86) * mm});
            skPoint(sketch, "E323.0", {"position": v(21.51, 9.33) * mm});
            skPoint(sketch, "E324.0", {"position": v(17.37, 9.58) * mm});
            skPoint(sketch, "E325.0", {"position": v(12.88, 9.65) * mm});
            skPoint(sketch, "E326.0", {"position": v(8.18, 9.59) * mm});
            skPoint(sketch, "E327.0", {"position": v(3.4, 9.42) * mm});
            skPoint(sketch, "E328.0", {"position": v(-14.33, 8.55) * mm});
            skPoint(sketch, "E329.0", {"position": v(-10.12, 8.78) * mm});
            skPoint(sketch, "E330.0", {"position": v(-5.9, 8.98) * mm});
            skPoint(sketch, "E331.0", {"position": v(-1.34, 9.2) * mm});
            skPoint(sketch, "E332.0", {"position": v(-19.1, 8.2) * mm});
            skPoint(sketch, "E333.0", {"position": v(-24.25, 7.73) * mm});
            skPoint(sketch, "E334.0", {"position": v(-29.6, 7.16) * mm});
            skPoint(sketch, "E335.0", {"position": v(-35, 6.5) * mm});
            skPoint(sketch, "E336.0", {"position": v(-40.24, 5.75) * mm});
            skPoint(sketch, "E337.0", {"position": v(-45.17, 4.92) * mm});
            skPoint(sketch, "E338.0", {"position": v(-49.6, 4.03) * mm});
            skPoint(sketch, "E339.0", {"position": v(-53.38, 3.07) * mm});
            skPoint(sketch, "E340.0", {"position": v(-56.31, 2.08) * mm});
            skPoint(sketch, "E341.0", {"position": v(-58.23, 1.04) * mm});
            skPoint(sketch, "E342.0", {"position": v(-58.96, -0.03) * mm});
            skPoint(sketch, "E343.0", {"position": v(-58.54, -1.04) * mm});
            skPoint(sketch, "E344.0", {"position": v(-57.22, -1.7) * mm});
            skPoint(sketch, "E345.0", {"position": v(-55.14, -2.02) * mm});
            skPoint(sketch, "E346.0", {"position": v(-49.2, -1.91) * mm});
            skPoint(sketch, "E347.0", {"position": v(-45.64, -1.57) * mm});
            skPoint(sketch, "E348.0", {"position": v(-41.85, -1.1) * mm});
            skPoint(sketch, "E349.0", {"position": v(-37.98, -0.57) * mm});
            skPoint(sketch, "E350.0", {"position": v(-34.17, 0) * mm});
            skPoint(sketch, "E351.0", {"position": v(-30.54, 0.55) * mm});
            skPoint(sketch, "E352.0", {"position": v(-27.24, 1.03) * mm});
            skPoint(sketch, "E353.0", {"position": v(-24.4, 1.4) * mm});
            skPoint(sketch, "E354.0", {"position": v(-20.27, 1.18) * mm});
            skPoint(sketch, "E355.0", {"position": v(-18.42, 0.62) * mm});
            skPoint(sketch, "E356.0", {"position": v(-16.71, -0.18) * mm});
            skPoint(sketch, "E357.0", {"position": v(-15.15, -1.14) * mm});
            skPoint(sketch, "E358.0", {"position": v(-22.27, 1.45) * mm});
            skPoint(sketch, "E359.0", {"position": v(-13.73, -2.24) * mm});
            skPoint(sketch, "E360.0", {"position": v(-12.46, -3.4) * mm});
            skPoint(sketch, "E361.0", {"position": v(-11.33, -4.59) * mm});
            skPoint(sketch, "E362.0", {"position": v(-10.34, -5.74) * mm});
            skPoint(sketch, "E363.0", {"position": v(-9.5, -6.8) * mm});
            skPoint(sketch, "E364.0", {"position": v(-8.8, -7.72) * mm});
            skPoint(sketch, "E365.0", {"position": v(-8.24, -8.44) * mm});
            skPoint(sketch, "E366.0", {"position": v(-8.81, -8.4) * mm});
            skPoint(sketch, "E367.0", {"position": v(-7.6, -9.13) * mm});
            skPoint(sketch, "E368.0", {"position": v(-6.87, -9.74) * mm});
            skPoint(sketch, "E369.0", {"position": v(-5.2, -10.7) * mm});
            skPoint(sketch, "E370.0", {"position": v(-6.06, -10.27) * mm});
            skPoint(sketch, "E371.0", {"position": v(-4.32, -11.02) * mm});
            skPoint(sketch, "E372.0", {"position": v(-3.44, -11.23) * mm});
            skPoint(sketch, "E373.0", {"position": v(-2.59, -11.32) * mm});
            skPoint(sketch, "E374.0", {"position": v(-1.8, -11.27) * mm});
            skPoint(sketch, "E375.0", {"position": v(-1.08, -11.09) * mm});
            skPoint(sketch, "E376.0", {"position": v(-0.47, -10.75) * mm});
            skPoint(sketch, "E377.0", {"position": v(0, -10.24) * mm});
            skPoint(sketch, "E378.0", {"position": v(0.31, -9.57) * mm});
            skPoint(sketch, "E379.0", {"position": v(0.6, -8.64) * mm});
            skPoint(sketch, "E380.0", {"position": v(0.9, -7.79) * mm});
            skPoint(sketch, "E381.0", {"position": v(1.18, -7) * mm});
            skPoint(sketch, "E382.0", {"position": v(1.44, -6.3) * mm});
            skPoint(sketch, "E383.0", {"position": v(1.67, -5.7) * mm});
            skPoint(sketch, "E384.0", {"position": v(1.84, -5.19) * mm});
            skPoint(sketch, "E385.0", {"position": v(1.95, -4.78) * mm});
            skPoint(sketch, "E386.0", {"position": v(1.98, -4.48) * mm});
            skPoint(sketch, "E387.0", {"position": v(1.92, -4.3) * mm});
            skPoint(sketch, "E388.0", {"position": v(1.48, -4.32) * mm});
            skPoint(sketch, "E389.0", {"position": v(1.08, -4.54) * mm});
            skPoint(sketch, "E390.0", {"position": v(0.17, -4.94) * mm});
            skPoint(sketch, "E391.0", {"position": v(-0.46, -4.93) * mm});
            skPoint(sketch, "E392.0", {"position": v(-0.84, -4.57) * mm});
            skPoint(sketch, "E393.0", {"position": v(-1, -3.93) * mm});
            skPoint(sketch, "E394.0", {"position": v(-0.98, -3.08) * mm});
            skPoint(sketch, "E395.0", {"position": v(-0.78, -2.1) * mm});
            skPoint(sketch, "E396.0", {"position": v(-0.45, -1.05) * mm});
            skPoint(sketch, "E397.0", {"position": v(0, 0) * mm});
            skPoint(sketch, "E398.0", {"position": v(0.54, 0.98) * mm});
            skPoint(sketch, "E399.0", {"position": v(1.13, 1.8) * mm});
            skPoint(sketch, "E400.0", {"position": v(1.76, 2.43) * mm});
            skPoint(sketch, "E401.0", {"position": v(2.4, 2.77) * mm});
            skPoint(sketch, "E402.0", {"position": v(3.48, 3.02) * mm});
            skPoint(sketch, "E403.0", {"position": v(4.6, 3.22) * mm});
            skLineSegment(sketch, "E404", {"start": v(-56.31, 2.08) * mm, "end": v(-53.38, 3.07) * mm});
            skLineSegment(sketch, "E405", {"start": v(-49.6, 4.03) * mm, "end": v(-53.38, 3.07) * mm});
            skLineSegment(sketch, "E406", {"start": v(-49.6, 4.03) * mm, "end": v(-45.17, 4.92) * mm});
            skLineSegment(sketch, "E407", {"start": v(-45.17, 4.92) * mm, "end": v(-40.24, 5.75) * mm});
            skLineSegment(sketch, "E408", {"start": v(-40.24, 5.75) * mm, "end": v(-35, 6.5) * mm});
            skLineSegment(sketch, "E409", {"start": v(-35, 6.5) * mm, "end": v(-29.6, 7.16) * mm});
            skLineSegment(sketch, "E410", {"start": v(-29.6, 7.16) * mm, "end": v(-24.25, 7.73) * mm});
            skLineSegment(sketch, "E411", {"start": v(-24.25, 7.73) * mm, "end": v(-19.1, 8.2) * mm});
            skLineSegment(sketch, "E412", {"start": v(-19.1, 8.2) * mm, "end": v(-14.33, 8.55) * mm});
            skLineSegment(sketch, "E413", {"start": v(-14.33, 8.55) * mm, "end": v(-10.12, 8.78) * mm});
            skLineSegment(sketch, "E414", {"start": v(-10.12, 8.78) * mm, "end": v(-5.9, 8.98) * mm});
            skLineSegment(sketch, "E415", {"start": v(-5.9, 8.98) * mm, "end": v(-1.34, 9.2) * mm});
            skLineSegment(sketch, "E416", {"start": v(-1.34, 9.2) * mm, "end": v(3.4, 9.42) * mm});
            skLineSegment(sketch, "E417", {"start": v(3.4, 9.42) * mm, "end": v(8.18, 9.59) * mm});
            skLineSegment(sketch, "E418", {"start": v(8.18, 9.59) * mm, "end": v(12.88, 9.65) * mm});
            skLineSegment(sketch, "E419", {"start": v(12.88, 9.65) * mm, "end": v(17.37, 9.58) * mm});
            skLineSegment(sketch, "E420", {"start": v(17.37, 9.58) * mm, "end": v(21.51, 9.33) * mm});
            skLineSegment(sketch, "E421", {"start": v(21.51, 9.33) * mm, "end": v(25.18, 8.86) * mm});
            skLineSegment(sketch, "E422", {"start": v(28.22, 8.13) * mm, "end": v(25.18, 8.86) * mm});
            skLineSegment(sketch, "E423", {"start": v(28.22, 8.13) * mm, "end": v(30.52, 7.1) * mm});
            skLineSegment(sketch, "E424", {"start": v(30.52, 7.1) * mm, "end": v(31.94, 5.71) * mm});
            skLineSegment(sketch, "E425", {"start": v(31.94, 5.71) * mm, "end": v(32.34, 3.95) * mm});
            skLineSegment(sketch, "E426", {"start": v(32.34, 3.95) * mm, "end": v(32.17, 2.36) * mm});
            skLineSegment(sketch, "E427", {"start": v(32.17, 2.36) * mm, "end": v(31.94, 1.04) * mm});
            skLineSegment(sketch, "E428", {"start": v(31.94, 1.04) * mm, "end": v(31.66, -0.02) * mm});
            skLineSegment(sketch, "E429", {"start": v(31.66, -0.02) * mm, "end": v(31.33, -0.85) * mm});
            skLineSegment(sketch, "E430", {"start": v(31.33, -0.85) * mm, "end": v(30.98, -1.47) * mm});
            skLineSegment(sketch, "E431", {"start": v(30.98, -1.47) * mm, "end": v(30.62, -1.89) * mm});
            skLineSegment(sketch, "E432", {"start": v(30.62, -1.89) * mm, "end": v(30.26, -2.13) * mm});
            skLineSegment(sketch, "E433", {"start": v(30.26, -2.13) * mm, "end": v(29.9, -2.22) * mm});
            skLineSegment(sketch, "E434", {"start": v(29.9, -2.22) * mm, "end": v(29.58, -2.16) * mm});
            skLineSegment(sketch, "E435", {"start": v(29.58, -2.16) * mm, "end": v(29.3, -2) * mm});
            skLineSegment(sketch, "E436", {"start": v(29.3, -2) * mm, "end": v(29.06, -1.72) * mm});
            skLineSegment(sketch, "E437", {"start": v(29.06, -1.72) * mm, "end": v(28.88, -1.37) * mm});
            skLineSegment(sketch, "E438", {"start": v(28.88, -1.37) * mm, "end": v(28.76, -1) * mm});
            skLineSegment(sketch, "E439", {"start": v(28.76, -1) * mm, "end": v(28.62, -0.55) * mm});
            skLineSegment(sketch, "E440", {"start": v(28.62, -0.55) * mm, "end": v(28.47, -0.07) * mm});
            skLineSegment(sketch, "E441", {"start": v(28.47, -0.07) * mm, "end": v(28.3, 0.43) * mm});
            skLineSegment(sketch, "E442", {"start": v(28.3, 0.43) * mm, "end": v(28.12, 0.94) * mm});
            skLineSegment(sketch, "E443", {"start": v(28.12, 0.94) * mm, "end": v(27.92, 1.45) * mm});
            skLineSegment(sketch, "E444", {"start": v(27.92, 1.45) * mm, "end": v(27.69, 1.92) * mm});
            skLineSegment(sketch, "E445", {"start": v(27.69, 1.92) * mm, "end": v(27.44, 2.35) * mm});
            skLineSegment(sketch, "E446", {"start": v(27.16, 2.72) * mm, "end": v(27.44, 2.35) * mm});
            skLineSegment(sketch, "E447", {"start": v(26.85, 3) * mm, "end": v(27.16, 2.72) * mm});
            skLineSegment(sketch, "E448", {"start": v(26.51, 3.2) * mm, "end": v(26.85, 3) * mm});
            skLineSegment(sketch, "E449", {"start": v(26.14, 3.27) * mm, "end": v(26.51, 3.2) * mm});
            skLineSegment(sketch, "E450", {"start": v(24.38, 3.33) * mm, "end": v(26.14, 3.27) * mm});
            skLineSegment(sketch, "E451", {"start": v(22.97, 3.37) * mm, "end": v(24.38, 3.33) * mm});
            skLineSegment(sketch, "E452", {"start": v(21.87, 3.4) * mm, "end": v(22.97, 3.37) * mm});
            skLineSegment(sketch, "E453", {"start": v(21, 3.42) * mm, "end": v(21.87, 3.4) * mm});
            skLineSegment(sketch, "E454", {"start": v(20.34, 3.43) * mm, "end": v(21, 3.42) * mm});
            skLineSegment(sketch, "E455", {"start": v(19.8, 3.43) * mm, "end": v(20.34, 3.43) * mm});
            skLineSegment(sketch, "E456", {"start": v(18.9, 3.43) * mm, "end": v(19.8, 3.43) * mm});
            skLineSegment(sketch, "E457", {"start": v(18.44, 3.43) * mm, "end": v(18.9, 3.43) * mm});
            skLineSegment(sketch, "E458", {"start": v(18.44, 3.43) * mm, "end": v(17.88, 3.43) * mm});
            skLineSegment(sketch, "E459", {"start": v(17.88, 3.43) * mm, "end": v(17.17, 3.43) * mm});
            skLineSegment(sketch, "E460", {"start": v(17.17, 3.43) * mm, "end": v(16.27, 3.44) * mm});
            skLineSegment(sketch, "E461", {"start": v(16.27, 3.44) * mm, "end": v(15.2, 3.46) * mm});
            skLineSegment(sketch, "E462", {"start": v(15.2, 3.46) * mm, "end": v(14.07, 3.48) * mm});
            skLineSegment(sketch, "E463", {"start": v(14.07, 3.48) * mm, "end": v(12.92, 3.51) * mm});
            skLineSegment(sketch, "E464", {"start": v(-1, -3.93) * mm, "end": v(-0.84, -4.57) * mm});
            skLineSegment(sketch, "E465", {"start": v(-0.84, -4.57) * mm, "end": v(-0.46, -4.93) * mm});
            skLineSegment(sketch, "E466", {"start": v(-0.46, -4.93) * mm, "end": v(0.17, -4.94) * mm});
            skLineSegment(sketch, "E467", {"start": v(0.17, -4.94) * mm, "end": v(1.08, -4.54) * mm});
            skLineSegment(sketch, "E468", {"start": v(1.08, -4.54) * mm, "end": v(1.48, -4.32) * mm});
            skLineSegment(sketch, "E469", {"start": v(1.48, -4.32) * mm, "end": v(1.92, -4.3) * mm});
            skLineSegment(sketch, "E470", {"start": v(1.92, -4.3) * mm, "end": v(1.98, -4.48) * mm});
            skLineSegment(sketch, "E471", {"start": v(1.98, -4.48) * mm, "end": v(1.95, -4.78) * mm});
            skLineSegment(sketch, "E472", {"start": v(1.95, -4.78) * mm, "end": v(1.84, -5.19) * mm});
            skLineSegment(sketch, "E473", {"start": v(1.84, -5.19) * mm, "end": v(1.67, -5.7) * mm});
            skLineSegment(sketch, "E474", {"start": v(1.67, -5.7) * mm, "end": v(1.44, -6.3) * mm});
            skLineSegment(sketch, "E475", {"start": v(1.44, -6.3) * mm, "end": v(1.18, -7) * mm});
            skLineSegment(sketch, "E476", {"start": v(1.18, -7) * mm, "end": v(0.9, -7.79) * mm});
            skLineSegment(sketch, "E477", {"start": v(-1, -3.93) * mm, "end": v(-0.98, -3.08) * mm});
            skLineSegment(sketch, "E478", {"start": v(-0.98, -3.08) * mm, "end": v(-0.78, -2.1) * mm});
            skLineSegment(sketch, "E479", {"start": v(-56.31, 2.08) * mm, "end": v(-58.23, 1.04) * mm});
            skLineSegment(sketch, "E480", {"start": v(-58.23, 1.04) * mm, "end": v(-58.96, -0.03) * mm});
            skLineSegment(sketch, "E481", {"start": v(-58.96, -0.03) * mm, "end": v(-58.54, -1.04) * mm});
            skLineSegment(sketch, "E482", {"start": v(-58.54, -1.04) * mm, "end": v(-57.22, -1.7) * mm});
            skLineSegment(sketch, "E483", {"start": v(-57.22, -1.7) * mm, "end": v(-55.14, -2.02) * mm});
            skLineSegment(sketch, "E484", {"start": v(-55.14, -2.02) * mm, "end": v(-49.2, -1.91) * mm});
            skLineSegment(sketch, "E485", {"start": v(-0.78, -2.1) * mm, "end": v(-0.45, -1.05) * mm});
            skLineSegment(sketch, "E486", {"start": v(0, 0) * mm, "end": v(-0.45, -1.05) * mm});
            skLineSegment(sketch, "E487", {"start": v(0, 0) * mm, "end": v(0.54, 0.98) * mm});
            skLineSegment(sketch, "E488", {"start": v(0.54, 0.98) * mm, "end": v(1.13, 1.8) * mm});
            skLineSegment(sketch, "E489", {"start": v(1.13, 1.8) * mm, "end": v(1.76, 2.43) * mm});
            skLineSegment(sketch, "E490", {"start": v(1.76, 2.43) * mm, "end": v(2.4, 2.77) * mm});
            skLineSegment(sketch, "E491", {"start": v(2.4, 2.77) * mm, "end": v(3.48, 3.02) * mm});
            skLineSegment(sketch, "E492", {"start": v(3.48, 3.02) * mm, "end": v(4.6, 3.22) * mm});
            skLineSegment(sketch, "E493", {"start": v(4.6, 3.22) * mm, "end": v(5.76, 3.36) * mm});
            skLineSegment(sketch, "E494", {"start": v(5.76, 3.36) * mm, "end": v(6.94, 3.46) * mm});
            skLineSegment(sketch, "E495", {"start": v(6.94, 3.46) * mm, "end": v(8.14, 3.52) * mm});
            skLineSegment(sketch, "E496", {"start": v(8.14, 3.52) * mm, "end": v(9.34, 3.55) * mm});
            skLineSegment(sketch, "E497", {"start": v(9.34, 3.55) * mm, "end": v(10.55, 3.56) * mm});
            skLineSegment(sketch, "E498", {"start": v(10.55, 3.56) * mm, "end": v(11.74, 3.54) * mm});
            skLineSegment(sketch, "E499", {"start": v(11.74, 3.54) * mm, "end": v(12.92, 3.51) * mm});
            skLineSegment(sketch, "E500", {"start": v(0.9, -7.79) * mm, "end": v(0.6, -8.64) * mm});
            skLineSegment(sketch, "E501", {"start": v(0.6, -8.64) * mm, "end": v(0.31, -9.57) * mm});
            skLineSegment(sketch, "E502", {"start": v(0.31, -9.57) * mm, "end": v(0, -10.24) * mm});
            skLineSegment(sketch, "E503", {"start": v(0, -10.24) * mm, "end": v(-0.47, -10.75) * mm});
            skLineSegment(sketch, "E504", {"start": v(-0.47, -10.75) * mm, "end": v(-1.08, -11.09) * mm});
            skLineSegment(sketch, "E505", {"start": v(-1.08, -11.09) * mm, "end": v(-1.8, -11.27) * mm});
            skLineSegment(sketch, "E506", {"start": v(-1.8, -11.27) * mm, "end": v(-2.59, -11.32) * mm});
            skLineSegment(sketch, "E507", {"start": v(-2.59, -11.32) * mm, "end": v(-3.44, -11.23) * mm});
            skLineSegment(sketch, "E508", {"start": v(-4.32, -11.02) * mm, "end": v(-3.44, -11.23) * mm});
            skLineSegment(sketch, "E509", {"start": v(-5.2, -10.7) * mm, "end": v(-4.32, -11.02) * mm});
            skLineSegment(sketch, "E510", {"start": v(-6.06, -10.27) * mm, "end": v(-5.2, -10.7) * mm});
            skLineSegment(sketch, "E511", {"start": v(-6.87, -9.74) * mm, "end": v(-6.06, -10.27) * mm});
            skLineSegment(sketch, "E512", {"start": v(-7.6, -9.13) * mm, "end": v(-6.87, -9.74) * mm});
            skLineSegment(sketch, "E513", {"start": v(-8.24, -8.44) * mm, "end": v(-7.6, -9.13) * mm});
            skLineSegment(sketch, "E514", {"start": v(-8.8, -7.72) * mm, "end": v(-8.24, -8.44) * mm});
            skLineSegment(sketch, "E515", {"start": v(-9.5, -6.8) * mm, "end": v(-8.8, -7.72) * mm});
            skLineSegment(sketch, "E516", {"start": v(-10.34, -5.74) * mm, "end": v(-9.5, -6.8) * mm});
            skLineSegment(sketch, "E517", {"start": v(-11.33, -4.59) * mm, "end": v(-10.34, -5.74) * mm});
            skLineSegment(sketch, "E518", {"start": v(-12.46, -3.4) * mm, "end": v(-11.33, -4.59) * mm});
            skLineSegment(sketch, "E519", {"start": v(-13.73, -2.24) * mm, "end": v(-12.46, -3.4) * mm});
            skLineSegment(sketch, "E520", {"start": v(-15.15, -1.14) * mm, "end": v(-13.73, -2.24) * mm});
            skLineSegment(sketch, "E521", {"start": v(-16.71, -0.18) * mm, "end": v(-15.15, -1.14) * mm});
            skLineSegment(sketch, "E522", {"start": v(-18.42, 0.62) * mm, "end": v(-16.71, -0.18) * mm});
            skLineSegment(sketch, "E523", {"start": v(-20.27, 1.18) * mm, "end": v(-18.42, 0.62) * mm});
            skLineSegment(sketch, "E524", {"start": v(-22.27, 1.45) * mm, "end": v(-20.27, 1.18) * mm});
            skLineSegment(sketch, "E525", {"start": v(-24.4, 1.4) * mm, "end": v(-22.27, 1.45) * mm});
            skLineSegment(sketch, "E526", {"start": v(-27.24, 1.03) * mm, "end": v(-24.4, 1.4) * mm});
            skLineSegment(sketch, "E527", {"start": v(-30.54, 0.55) * mm, "end": v(-27.24, 1.03) * mm});
            skLineSegment(sketch, "E528", {"start": v(-34.17, 0) * mm, "end": v(-30.54, 0.55) * mm});
            skLineSegment(sketch, "E529", {"start": v(-37.98, -0.57) * mm, "end": v(-34.17, 0) * mm});
            skLineSegment(sketch, "E530", {"start": v(-41.85, -1.1) * mm, "end": v(-37.98, -0.57) * mm});
            skLineSegment(sketch, "E531", {"start": v(-45.64, -1.57) * mm, "end": v(-41.85, -1.1) * mm});
            skLineSegment(sketch, "E532", {"start": v(-49.2, -1.91) * mm, "end": v(-45.64, -1.57) * mm});
            skLineSegment(sketch, "E533.0", {"start": v(12.85, 7.65) * mm, "end": v(17.3, 7.58) * mm});
            skLineSegment(sketch, "E533.1", {"start": v(17.3, 7.58) * mm, "end": v(21.33, 7.34) * mm});
            skLineSegment(sketch, "E533.2", {"start": v(29.38, 5.42) * mm, "end": v(30.54, 4.28) * mm});
            skLineSegment(sketch, "E533.3", {"start": v(27.57, 6.23) * mm, "end": v(29.38, 5.42) * mm});
            skLineSegment(sketch, "E533.4", {"start": v(27.57, 6.23) * mm, "end": v(24.81, 6.9) * mm});
            skLineSegment(sketch, "E533.5", {"start": v(21.33, 7.34) * mm, "end": v(24.81, 6.9) * mm});
            skLineSegment(sketch, "E534.0", {"start": v(-1.25, 7.21) * mm, "end": v(3.48, 7.43) * mm});
            skLineSegment(sketch, "E534.1", {"start": v(-5.8, 6.98) * mm, "end": v(-1.25, 7.21) * mm});
            skLineSegment(sketch, "E534.2", {"start": v(-24.07, 5.74) * mm, "end": v(-18.93, 6.2) * mm});
            skLineSegment(sketch, "E534.3", {"start": v(-18.93, 6.2) * mm, "end": v(-14.2, 6.56) * mm});
            skLineSegment(sketch, "E534.4", {"start": v(-14.2, 6.56) * mm, "end": v(-10.02, 6.78) * mm});
            skLineSegment(sketch, "E534.5", {"start": v(-10.02, 6.78) * mm, "end": v(-5.8, 6.98) * mm});
            skLineSegment(sketch, "E535.0", {"start": v(8.22, 7.59) * mm, "end": v(12.9, 7.65) * mm});
            skLineSegment(sketch, "E535.1", {"start": v(3.46, 7.43) * mm, "end": v(8.22, 7.59) * mm});
            skLineSegment(sketch, "E536.0", {"start": v(-29.37, 5.18) * mm, "end": v(-24.03, 5.75) * mm});
            skLineSegment(sketch, "E536.1", {"start": v(-34.73, 4.52) * mm, "end": v(-29.37, 5.18) * mm});
            skLineSegment(sketch, "E536.2", {"start": v(-39.95, 3.77) * mm, "end": v(-34.73, 4.52) * mm});
            skLineSegment(sketch, "E537.0", {"start": v(-44.8, 2.95) * mm, "end": v(-39.9, 3.77) * mm});
            skLineSegment(sketch, "E537.1", {"start": v(-49.16, 2.08) * mm, "end": v(-44.8, 2.95) * mm});
            skLineSegment(sketch, "E537.2", {"start": v(-49.16, 2.08) * mm, "end": v(-52.9, 1.14) * mm});
            skLineSegment(sketch, "E538.0", {"start": v(-55.5, 0.24) * mm, "end": v(-52.73, 1.18) * mm});
            skLineSegment(sketch, "E538.1", {"start": v(-55.5, 0.24) * mm, "end": v(-56.2, -0.14) * mm});
            skLineSegment(sketch, "E539", {"start": v(30.54, 4.28) * mm, "end": v(26.81, 4.28) * mm});
            skLineSegment(sketch, "E540", {"start": v(26.81, 4.28) * mm, "end": v(-4.07, 4.28) * mm});
            skLineSegment(sketch, "E541", {"start": v(-4.07, 4.28) * mm, "end": v(-40.78, 0.96) * mm});
            skLineSegment(sketch, "E542", {"start": v(-40.78, 0.96) * mm, "end": v(-56.2, -0.14) * mm});
            skLineSegment(sketch, "E543", {"start": v(-44.8, 2.95) * mm, "end": v(-44.64, 0.68) * mm});
            skPoint(sketch, "E544.start.orphan", {"position": v(-37.34, 4.14) * mm});
            skSolve(sketch);
        }
        {
            var Q0;
            {var subQ5=sQuery(id+"F8.wireOp",EDGE,"E533.1");Q0=makeQuery(id+"F8.imprint","IMPRINT",FACE,{"disambiguationData":[TD([[makeQuery(id+"F8.imprint","IMPRINT",EDGE,{"derivedFrom":subQ5}),-1.0]])]});}
            extrude(context, id + "F9", {"entities" : qUnion([Q0]), "operationType" : NewBodyOperationType.ADD, "endBound" : BoundingType.SYMMETRIC, "depth" : 9 * mm});
        }
        {
            var Q0;
            Q0=makeQuery(id+"F9.opExtrude","SWEPT_BODY",BODY,{"disambiguationData":[OSD([sQuery(id+"F8.wireOp",EDGE,"E533.0"),sQuery(id+"F8.wireOp",EDGE,"E533.1"),sQuery(id+"F8.wireOp",EDGE,"E533.2"),sQuery(id+"F8.wireOp",EDGE,"E533.3"),sQuery(id+"F8.wireOp",EDGE,"E533.4"),sQuery(id+"F8.wireOp",EDGE,"E533.5"),sQuery(id+"F8.wireOp",EDGE,"E534.0"),sQuery(id+"F8.wireOp",EDGE,"E534.1"),sQuery(id+"F8.wireOp",EDGE,"E534.2"),sQuery(id+"F8.wireOp",EDGE,"E534.3"),sQuery(id+"F8.wireOp",EDGE,"E534.4"),sQuery(id+"F8.wireOp",EDGE,"E534.5"),sQuery(id+"F8.wireOp",EDGE,"E535.0"),sQuery(id+"F8.wireOp",EDGE,"E535.1"),sQuery(id+"F8.wireOp",EDGE,"E536.0"),sQuery(id+"F8.wireOp",EDGE,"E536.1"),sQuery(id+"F8.wireOp",EDGE,"E536.2"),sQuery(id+"F8.wireOp",EDGE,"E539"),sQuery(id+"F8.wireOp",EDGE,"E540"),sQuery(id+"F8.wireOp",EDGE,"E541"),sQuery(id+"F8.wireOp",EDGE,"E544")])]});
            var Q1;
            Q1=sQuery(id+"F0.wireOp",EDGE,"E259");
            transform(context, id + "F10", {"entities" : qUnion([Q0]), "transformType" : TransformType.ROTATION, "transformAxis" : qUnion([Q1]), "angle" : 180 * degree, "makeCopy" : false});
        }
        {
            var Q0;
            Q0=makeQuery(id+"F9.opExtrude","SWEPT_BODY",BODY,{"disambiguationData":[OSD([sQuery(id+"F8.wireOp",EDGE,"E533.0"),sQuery(id+"F8.wireOp",EDGE,"E533.1"),sQuery(id+"F8.wireOp",EDGE,"E533.2"),sQuery(id+"F8.wireOp",EDGE,"E533.3"),sQuery(id+"F8.wireOp",EDGE,"E533.4"),sQuery(id+"F8.wireOp",EDGE,"E533.5"),sQuery(id+"F8.wireOp",EDGE,"E534.0"),sQuery(id+"F8.wireOp",EDGE,"E534.1"),sQuery(id+"F8.wireOp",EDGE,"E534.2"),sQuery(id+"F8.wireOp",EDGE,"E534.3"),sQuery(id+"F8.wireOp",EDGE,"E534.4"),sQuery(id+"F8.wireOp",EDGE,"E534.5"),sQuery(id+"F8.wireOp",EDGE,"E535.0"),sQuery(id+"F8.wireOp",EDGE,"E535.1"),sQuery(id+"F8.wireOp",EDGE,"E536.0"),sQuery(id+"F8.wireOp",EDGE,"E536.1"),sQuery(id+"F8.wireOp",EDGE,"E536.2"),sQuery(id+"F8.wireOp",EDGE,"E537.0"),sQuery(id+"F8.wireOp",EDGE,"E539"),sQuery(id+"F8.wireOp",EDGE,"E540"),sQuery(id+"F8.wireOp",EDGE,"E541"),sQuery(id+"F8.wireOp",EDGE,"E542"),sQuery(id+"F8.wireOp",EDGE,"E543")])]});
            var Q1;
            Q1=makeQuery(id+"F1.opExtrude","SWEPT_BODY",BODY,{"disambiguationData":[OSD([sQuery(id+"F0.wireOp",EDGE,"E130"),sQuery(id+"F0.wireOp",EDGE,"E131"),sQuery(id+"F0.wireOp",EDGE,"E132"),sQuery(id+"F0.wireOp",EDGE,"E133"),sQuery(id+"F0.wireOp",EDGE,"E134"),sQuery(id+"F0.wireOp",EDGE,"E135"),sQuery(id+"F0.wireOp",EDGE,"E136"),sQuery(id+"F0.wireOp",EDGE,"E137"),sQuery(id+"F0.wireOp",EDGE,"E138"),sQuery(id+"F0.wireOp",EDGE,"E139"),sQuery(id+"F0.wireOp",EDGE,"E140"),sQuery(id+"F0.wireOp",EDGE,"E141"),sQuery(id+"F0.wireOp",EDGE,"E142"),sQuery(id+"F0.wireOp",EDGE,"E143"),sQuery(id+"F0.wireOp",EDGE,"E144"),sQuery(id+"F0.wireOp",EDGE,"E145"),sQuery(id+"F0.wireOp",EDGE,"E146"),sQuery(id+"F0.wireOp",EDGE,"E147"),sQuery(id+"F0.wireOp",EDGE,"E148"),sQuery(id+"F0.wireOp",EDGE,"E149"),sQuery(id+"F0.wireOp",EDGE,"E150"),sQuery(id+"F0.wireOp",EDGE,"E151"),sQuery(id+"F0.wireOp",EDGE,"E152"),sQuery(id+"F0.wireOp",EDGE,"E153"),sQuery(id+"F0.wireOp",EDGE,"E154"),sQuery(id+"F0.wireOp",EDGE,"E155"),sQuery(id+"F0.wireOp",EDGE,"E156"),sQuery(id+"F0.wireOp",EDGE,"E157"),sQuery(id+"F0.wireOp",EDGE,"E158"),sQuery(id+"F0.wireOp",EDGE,"E159"),sQuery(id+"F0.wireOp",EDGE,"E160"),sQuery(id+"F0.wireOp",EDGE,"E161"),sQuery(id+"F0.wireOp",EDGE,"E162"),sQuery(id+"F0.wireOp",EDGE,"E163"),sQuery(id+"F0.wireOp",EDGE,"E164"),sQuery(id+"F0.wireOp",EDGE,"E165"),sQuery(id+"F0.wireOp",EDGE,"E166"),sQuery(id+"F0.wireOp",EDGE,"E167"),sQuery(id+"F0.wireOp",EDGE,"E168"),sQuery(id+"F0.wireOp",EDGE,"E169"),sQuery(id+"F0.wireOp",EDGE,"E170"),sQuery(id+"F0.wireOp",EDGE,"E171"),sQuery(id+"F0.wireOp",EDGE,"E172"),sQuery(id+"F0.wireOp",EDGE,"E173"),sQuery(id+"F0.wireOp",EDGE,"E174"),sQuery(id+"F0.wireOp",EDGE,"E175"),sQuery(id+"F0.wireOp",EDGE,"E176"),sQuery(id+"F0.wireOp",EDGE,"E177"),sQuery(id+"F0.wireOp",EDGE,"E178"),sQuery(id+"F0.wireOp",EDGE,"E179"),sQuery(id+"F0.wireOp",EDGE,"E180"),sQuery(id+"F0.wireOp",EDGE,"E181"),sQuery(id+"F0.wireOp",EDGE,"E182"),sQuery(id+"F0.wireOp",EDGE,"E183"),sQuery(id+"F0.wireOp",EDGE,"E184"),sQuery(id+"F0.wireOp",EDGE,"E185"),sQuery(id+"F0.wireOp",EDGE,"E186"),sQuery(id+"F0.wireOp",EDGE,"E187"),sQuery(id+"F0.wireOp",EDGE,"E188"),sQuery(id+"F0.wireOp",EDGE,"E189"),sQuery(id+"F0.wireOp",EDGE,"E190"),sQuery(id+"F0.wireOp",EDGE,"E191"),sQuery(id+"F0.wireOp",EDGE,"E192"),sQuery(id+"F0.wireOp",EDGE,"E193"),sQuery(id+"F0.wireOp",EDGE,"E194"),sQuery(id+"F0.wireOp",EDGE,"E195"),sQuery(id+"F0.wireOp",EDGE,"E196"),sQuery(id+"F0.wireOp",EDGE,"E197"),sQuery(id+"F0.wireOp",EDGE,"E198"),sQuery(id+"F0.wireOp",EDGE,"E199"),sQuery(id+"F0.wireOp",EDGE,"E200"),sQuery(id+"F0.wireOp",EDGE,"E201"),sQuery(id+"F0.wireOp",EDGE,"E202"),sQuery(id+"F0.wireOp",EDGE,"E203"),sQuery(id+"F0.wireOp",EDGE,"E204"),sQuery(id+"F0.wireOp",EDGE,"E205"),sQuery(id+"F0.wireOp",EDGE,"E206"),sQuery(id+"F0.wireOp",EDGE,"E207"),sQuery(id+"F0.wireOp",EDGE,"E208"),sQuery(id+"F0.wireOp",EDGE,"E209"),sQuery(id+"F0.wireOp",EDGE,"E210"),sQuery(id+"F0.wireOp",EDGE,"E211"),sQuery(id+"F0.wireOp",EDGE,"E212"),sQuery(id+"F0.wireOp",EDGE,"E213"),sQuery(id+"F0.wireOp",EDGE,"E214"),sQuery(id+"F0.wireOp",EDGE,"E215"),sQuery(id+"F0.wireOp",EDGE,"E216"),sQuery(id+"F0.wireOp",EDGE,"E217"),sQuery(id+"F0.wireOp",EDGE,"E218"),sQuery(id+"F0.wireOp",EDGE,"E219"),sQuery(id+"F0.wireOp",EDGE,"E220"),sQuery(id+"F0.wireOp",EDGE,"E221"),sQuery(id+"F0.wireOp",EDGE,"E222"),sQuery(id+"F0.wireOp",EDGE,"E223"),sQuery(id+"F0.wireOp",EDGE,"E224"),sQuery(id+"F0.wireOp",EDGE,"E225"),sQuery(id+"F0.wireOp",EDGE,"E226"),sQuery(id+"F0.wireOp",EDGE,"E227"),sQuery(id+"F0.wireOp",EDGE,"E228"),sQuery(id+"F0.wireOp",EDGE,"E229"),sQuery(id+"F0.wireOp",EDGE,"E230"),sQuery(id+"F0.wireOp",EDGE,"E231"),sQuery(id+"F0.wireOp",EDGE,"E232"),sQuery(id+"F0.wireOp",EDGE,"E233"),sQuery(id+"F0.wireOp",EDGE,"E234"),sQuery(id+"F0.wireOp",EDGE,"E235"),sQuery(id+"F0.wireOp",EDGE,"E236"),sQuery(id+"F0.wireOp",EDGE,"E237"),sQuery(id+"F0.wireOp",EDGE,"E238"),sQuery(id+"F0.wireOp",EDGE,"E239"),sQuery(id+"F0.wireOp",EDGE,"E240"),sQuery(id+"F0.wireOp",EDGE,"E241"),sQuery(id+"F0.wireOp",EDGE,"E242"),sQuery(id+"F0.wireOp",EDGE,"E243"),sQuery(id+"F0.wireOp",EDGE,"E244"),sQuery(id+"F0.wireOp",EDGE,"E245"),sQuery(id+"F0.wireOp",EDGE,"E246"),sQuery(id+"F0.wireOp",EDGE,"E247"),sQuery(id+"F0.wireOp",EDGE,"E248"),sQuery(id+"F0.wireOp",EDGE,"E249"),sQuery(id+"F0.wireOp",EDGE,"E250"),sQuery(id+"F0.wireOp",EDGE,"E251"),sQuery(id+"F0.wireOp",EDGE,"E252"),sQuery(id+"F0.wireOp",EDGE,"E253"),sQuery(id+"F0.wireOp",EDGE,"E254"),sQuery(id+"F0.wireOp",EDGE,"E255"),sQuery(id+"F0.wireOp",EDGE,"E256"),sQuery(id+"F0.wireOp",EDGE,"E257"),sQuery(id+"F0.wireOp",EDGE,"E258")])]});
            booleanBodies(context, id + "F11", {"operationType" : BooleanOperationType.UNION, "tools" : qUnion([Q0, Q1])});
        }
        {
            var Q0;
            Q0=makeQuery(id+"F5.boolean.opBoolean","INTERSECT",EDGE,{"derivedFrom":[makeQuery(id+"F1.opExtrude","SWEPT_FACE",FACE,{"disambiguationData":[OSD([sQuery(id+"F0.wireOp",EDGE,"E210")])]}),makeQuery(id+"F5.opExtrude","SWEPT_FACE",FACE,{"disambiguationData":[OSD([sQuery(id+"F4.wireOp",EDGE,"E267")])]})]});
            var Q1;
            Q1=makeQuery(id+"F5.boolean.opBoolean","INTERSECT",EDGE,{"derivedFrom":[makeQuery(id+"F1.opExtrude","SWEPT_FACE",FACE,{"disambiguationData":[OSD([sQuery(id+"F0.wireOp",EDGE,"E131")])]}),makeQuery(id+"F5.opExtrude","SWEPT_FACE",FACE,{"disambiguationData":[OSD([sQuery(id+"F4.wireOp",EDGE,"E267")])]})]});
            var Q2;
            Q2=makeQuery(id+"F5.boolean.opBoolean","INTERSECT",EDGE,{"derivedFrom":[makeQuery(id+"F1.opExtrude","SWEPT_FACE",FACE,{"disambiguationData":[OSD([sQuery(id+"F0.wireOp",EDGE,"E132")])]}),makeQuery(id+"F5.opExtrude","SWEPT_FACE",FACE,{"disambiguationData":[OSD([sQuery(id+"F4.wireOp",EDGE,"E267")])]})]});
            var Q3;
            Q3=makeQuery(id+"F5.boolean.opBoolean","INTERSECT",EDGE,{"derivedFrom":[makeQuery(id+"F1.opExtrude","SWEPT_FACE",FACE,{"disambiguationData":[OSD([sQuery(id+"F0.wireOp",EDGE,"E258")])]}),makeQuery(id+"F5.opExtrude","SWEPT_FACE",FACE,{"disambiguationData":[OSD([sQuery(id+"F4.wireOp",EDGE,"E267")])]})]});
            fillet(context, id + "F12", {"entities" : qUnion([Q0, Q1, Q2, Q3]), "radius" : 1 * mm, "tangentPropagation" : true, "allowEdgeOverflow" : false});
        }
        {
            var Q0;
            Q0=makeQuery(id+"F11.opBoolean","INTERSECT",EDGE,{"derivedFrom":[makeQuery(id+"F7.boolean.opBoolean","COPY",FACE,{"derivedFrom":makeQuery(id+"F7.opExtrude","SWEPT_FACE",FACE,{"disambiguationData":[OSD([sQuery(id+"F4.wireOp",EDGE,"E270.sketch_text.stroke-1")])]})}),makeQuery(id+"F9.opExtrude","SWEPT_FACE",FACE,{"disambiguationData":[OSD([sQuery(id+"F8.wireOp",EDGE,"E537.0")])]})]});
            var Q1;
            Q1=makeQuery(id+"F11.opBoolean","INTERSECT",EDGE,{"derivedFrom":[makeQuery(id+"F7.boolean.opBoolean","COPY",FACE,{"derivedFrom":makeQuery(id+"F7.opExtrude","SWEPT_FACE",FACE,{"disambiguationData":[OSD([sQuery(id+"F4.wireOp",EDGE,"E270.sketch_text.stroke-1")])]})}),makeQuery(id+"F9.opExtrude","SWEPT_FACE",FACE,{"disambiguationData":[OSD([sQuery(id+"F8.wireOp",EDGE,"E536.2")])]})]});
            var Q2;
            Q2=makeQuery(id+"F11.opBoolean","INTERSECT",EDGE,{"derivedFrom":[makeQuery(id+"F7.boolean.opBoolean","COPY",FACE,{"derivedFrom":makeQuery(id+"F7.opExtrude","SWEPT_FACE",FACE,{"disambiguationData":[OSD([sQuery(id+"F4.wireOp",EDGE,"E270.sketch_text.stroke-14")])]})}),makeQuery(id+"F9.opExtrude","SWEPT_FACE",FACE,{"disambiguationData":[OSD([sQuery(id+"F8.wireOp",EDGE,"E536.1")])]})]});
            var Q3;
            Q3=makeQuery(id+"F11.opBoolean","INTERSECT",EDGE,{"derivedFrom":[makeQuery(id+"F7.boolean.opBoolean","COPY",FACE,{"derivedFrom":makeQuery(id+"F7.opExtrude","SWEPT_FACE",FACE,{"disambiguationData":[OSD([sQuery(id+"F4.wireOp",EDGE,"E270.sketch_text.stroke-41")])]})}),makeQuery(id+"F9.opExtrude","SWEPT_FACE",FACE,{"disambiguationData":[OSD([sQuery(id+"F8.wireOp",EDGE,"E536.0")])]})]});
            var Q4;
            Q4=makeQuery(id+"F11.opBoolean","INTERSECT",EDGE,{"derivedFrom":[makeQuery(id+"F7.boolean.opBoolean","COPY",FACE,{"derivedFrom":makeQuery(id+"F7.opExtrude","SWEPT_FACE",FACE,{"disambiguationData":[OSD([sQuery(id+"F4.wireOp",EDGE,"E270.sketch_text.stroke-8")])]})}),makeQuery(id+"F9.opExtrude","SWEPT_FACE",FACE,{"disambiguationData":[OSD([sQuery(id+"F8.wireOp",EDGE,"E536.1")])]})]});
            var Q5;
            Q5=makeQuery(id+"F11.opBoolean","INTERSECT",EDGE,{"derivedFrom":[makeQuery(id+"F6.boolean.opBoolean","COPY",FACE,{"derivedFrom":makeQuery(id+"F6.opExtrude","SWEPT_FACE",FACE,{"disambiguationData":[OSD([sQuery(id+"F4.wireOp",EDGE,"E270.sketch_text.stroke-54")])]})}),makeQuery(id+"F9.opExtrude","SWEPT_FACE",FACE,{"disambiguationData":[OSD([sQuery(id+"F8.wireOp",EDGE,"E534.3")])]})]});
            var Q6;
            Q6=makeQuery(id+"F11.opBoolean","INTERSECT",EDGE,{"derivedFrom":[makeQuery(id+"F6.boolean.opBoolean","COPY",FACE,{"derivedFrom":makeQuery(id+"F6.opExtrude","SWEPT_FACE",FACE,{"disambiguationData":[OSD([sQuery(id+"F4.wireOp",EDGE,"E270.sketch_text.stroke-69")])]})}),makeQuery(id+"F9.opExtrude","SWEPT_FACE",FACE,{"disambiguationData":[OSD([sQuery(id+"F8.wireOp",EDGE,"E534.4")])]})]});
            var Q7;
            Q7=makeQuery(id+"F11.opBoolean","INTERSECT",EDGE,{"derivedFrom":[makeQuery(id+"F6.boolean.opBoolean","COPY",FACE,{"derivedFrom":makeQuery(id+"F6.opExtrude","SWEPT_FACE",FACE,{"disambiguationData":[OSD([sQuery(id+"F4.wireOp",EDGE,"E270.sketch_text.stroke-73")])]})}),makeQuery(id+"F9.opExtrude","SWEPT_FACE",FACE,{"disambiguationData":[OSD([sQuery(id+"F8.wireOp",EDGE,"E534.4")])]})]});
            var Q8;
            Q8=makeQuery(id+"F11.opBoolean","INTERSECT",EDGE,{"derivedFrom":[makeQuery(id+"F6.boolean.opBoolean","COPY",FACE,{"derivedFrom":makeQuery(id+"F6.opExtrude","SWEPT_FACE",FACE,{"disambiguationData":[OSD([sQuery(id+"F4.wireOp",EDGE,"E270.sketch_text.stroke-76")])]})}),makeQuery(id+"F9.opExtrude","SWEPT_FACE",FACE,{"disambiguationData":[OSD([sQuery(id+"F8.wireOp",EDGE,"E534.5")])]})]});
            var Q9;
            Q9=makeQuery(id+"F11.opBoolean","INTERSECT",EDGE,{"derivedFrom":[makeQuery(id+"F6.boolean.opBoolean","COPY",FACE,{"derivedFrom":makeQuery(id+"F6.opExtrude","SWEPT_FACE",FACE,{"disambiguationData":[OSD([sQuery(id+"F4.wireOp",EDGE,"E270.sketch_text.stroke-87")])]})}),makeQuery(id+"F9.opExtrude","SWEPT_FACE",FACE,{"disambiguationData":[OSD([sQuery(id+"F8.wireOp",EDGE,"E534.5")])]})]});
            var Q10;
            Q10=makeQuery(id+"F11.opBoolean","INTERSECT",EDGE,{"derivedFrom":[makeQuery(id+"F6.boolean.opBoolean","COPY",FACE,{"derivedFrom":makeQuery(id+"F6.opExtrude","SWEPT_FACE",FACE,{"disambiguationData":[OSD([sQuery(id+"F4.wireOp",EDGE,"E270.sketch_text.stroke-91")])]})}),makeQuery(id+"F9.opExtrude","SWEPT_FACE",FACE,{"disambiguationData":[OSD([sQuery(id+"F8.wireOp",EDGE,"E534.1")])]})]});
            var Q11;
            Q11=makeQuery(id+"F11.opBoolean","INTERSECT",EDGE,{"derivedFrom":[makeQuery(id+"F6.boolean.opBoolean","COPY",FACE,{"derivedFrom":makeQuery(id+"F6.opExtrude","SWEPT_FACE",FACE,{"disambiguationData":[OSD([sQuery(id+"F4.wireOp",EDGE,"E270.sketch_text.stroke-89")])]})}),makeQuery(id+"F9.opExtrude","SWEPT_FACE",FACE,{"disambiguationData":[OSD([sQuery(id+"F8.wireOp",EDGE,"E534.1")])]})]});
            var Q12;
            Q12=makeQuery(id+"F11.opBoolean","INTERSECT",EDGE,{"derivedFrom":[makeQuery(id+"F6.boolean.opBoolean","COPY",FACE,{"derivedFrom":makeQuery(id+"F6.opExtrude","SWEPT_FACE",FACE,{"disambiguationData":[OSD([sQuery(id+"F4.wireOp",EDGE,"E270.sketch_text.stroke-99")])]})}),makeQuery(id+"F9.opExtrude","SWEPT_FACE",FACE,{"disambiguationData":[OSD([sQuery(id+"F8.wireOp",EDGE,"E534.0")])]})]});
            var Q13;
            Q13=makeQuery(id+"F11.opBoolean","INTERSECT",EDGE,{"derivedFrom":[makeQuery(id+"F6.boolean.opBoolean","COPY",FACE,{"derivedFrom":makeQuery(id+"F6.opExtrude","SWEPT_FACE",FACE,{"disambiguationData":[OSD([sQuery(id+"F4.wireOp",EDGE,"E270.sketch_text.stroke-109")])]})}),makeQuery(id+"F9.opExtrude","SWEPT_FACE",FACE,{"disambiguationData":[OSD([sQuery(id+"F8.wireOp",EDGE,"E535.1")])]})]});
            var Q14;
            Q14=makeQuery(id+"F11.opBoolean","INTERSECT",EDGE,{"derivedFrom":[makeQuery(id+"F6.boolean.opBoolean","COPY",FACE,{"derivedFrom":makeQuery(id+"F6.opExtrude","SWEPT_FACE",FACE,{"disambiguationData":[OSD([sQuery(id+"F4.wireOp",EDGE,"E270.sketch_text.stroke-103")])]})}),makeQuery(id+"F9.opExtrude","SWEPT_FACE",FACE,{"disambiguationData":[OSD([sQuery(id+"F8.wireOp",EDGE,"E535.1")])]})]});
            var Q15;
            Q15=makeQuery(id+"F11.opBoolean","INTERSECT",EDGE,{"derivedFrom":[makeQuery(id+"F6.boolean.opBoolean","COPY",FACE,{"derivedFrom":makeQuery(id+"F6.opExtrude","SWEPT_FACE",FACE,{"disambiguationData":[OSD([sQuery(id+"F4.wireOp",EDGE,"E270.sketch_text.stroke-115")])]})}),makeQuery(id+"F9.opExtrude","SWEPT_FACE",FACE,{"disambiguationData":[OSD([sQuery(id+"F8.wireOp",EDGE,"E535.1")])]})]});
            var Q16;
            Q16=makeQuery(id+"F11.opBoolean","INTERSECT",EDGE,{"derivedFrom":[makeQuery(id+"F7.boolean.opBoolean","COPY",FACE,{"derivedFrom":makeQuery(id+"F7.opExtrude","SWEPT_FACE",FACE,{"disambiguationData":[OSD([sQuery(id+"F4.wireOp",EDGE,"E270.sketch_text.stroke-20")])]})}),makeQuery(id+"F9.opExtrude","SWEPT_FACE",FACE,{"disambiguationData":[OSD([sQuery(id+"F8.wireOp",EDGE,"E536.1")])]})]});
            var Q17;
            Q17=makeQuery(id+"F11.opBoolean","INTERSECT",EDGE,{"derivedFrom":[makeQuery(id+"F6.boolean.opBoolean","COPY",FACE,{"derivedFrom":makeQuery(id+"F6.opExtrude","SWEPT_FACE",FACE,{"disambiguationData":[OSD([sQuery(id+"F4.wireOp",EDGE,"E270.sketch_text.stroke-128")])]})}),makeQuery(id+"F9.opExtrude","SWEPT_FACE",FACE,{"disambiguationData":[OSD([sQuery(id+"F8.wireOp",EDGE,"E535.0")])]})]});
            var Q18;
            Q18=makeQuery(id+"F11.opBoolean","INTERSECT",EDGE,{"derivedFrom":[makeQuery(id+"F6.boolean.opBoolean","COPY",FACE,{"derivedFrom":makeQuery(id+"F6.opExtrude","SWEPT_FACE",FACE,{"disambiguationData":[OSD([sQuery(id+"F4.wireOp",EDGE,"E270.sketch_text.stroke-135")])]})}),makeQuery(id+"F9.opExtrude","SWEPT_FACE",FACE,{"disambiguationData":[OSD([sQuery(id+"F8.wireOp",EDGE,"E533.0")])]})]});
            var Q19;
            Q19=makeQuery(id+"F11.opBoolean","INTERSECT",EDGE,{"derivedFrom":[makeQuery(id+"F6.boolean.opBoolean","COPY",FACE,{"derivedFrom":makeQuery(id+"F6.opExtrude","SWEPT_FACE",FACE,{"disambiguationData":[OSD([sQuery(id+"F4.wireOp",EDGE,"E270.sketch_text.stroke-132")])]})}),makeQuery(id+"F9.opExtrude","SWEPT_FACE",FACE,{"disambiguationData":[OSD([sQuery(id+"F8.wireOp",EDGE,"E535.0")])]})]});
            var Q20;
            Q20=makeQuery(id+"F11.opBoolean","INTERSECT",EDGE,{"derivedFrom":[makeQuery(id+"F6.boolean.opBoolean","COPY",FACE,{"derivedFrom":makeQuery(id+"F6.opExtrude","SWEPT_FACE",FACE,{"disambiguationData":[OSD([sQuery(id+"F4.wireOp",EDGE,"E270.sketch_text.stroke-139")])]})}),makeQuery(id+"F9.opExtrude","SWEPT_FACE",FACE,{"disambiguationData":[OSD([sQuery(id+"F8.wireOp",EDGE,"E533.0")])]})]});
            var Q21;
            Q21=makeQuery(id+"F11.opBoolean","INTERSECT",EDGE,{"derivedFrom":[makeQuery(id+"F6.boolean.opBoolean","COPY",FACE,{"derivedFrom":makeQuery(id+"F6.opExtrude","SWEPT_FACE",FACE,{"disambiguationData":[OSD([sQuery(id+"F4.wireOp",EDGE,"E270.sketch_text.stroke-142")])]})}),makeQuery(id+"F9.opExtrude","SWEPT_FACE",FACE,{"disambiguationData":[OSD([sQuery(id+"F8.wireOp",EDGE,"E533.1")])]})]});
            var Q22;
            Q22=makeQuery(id+"F11.opBoolean","INTERSECT",EDGE,{"derivedFrom":[makeQuery(id+"F6.boolean.opBoolean","COPY",FACE,{"derivedFrom":makeQuery(id+"F6.opExtrude","SWEPT_FACE",FACE,{"disambiguationData":[OSD([sQuery(id+"F4.wireOp",EDGE,"E270.sketch_text.stroke-141")])]})}),makeQuery(id+"F9.opExtrude","SWEPT_FACE",FACE,{"disambiguationData":[OSD([sQuery(id+"F8.wireOp",EDGE,"E533.1")])]})]});
            var Q23;
            Q23=makeQuery(id+"F11.opBoolean","INTERSECT",EDGE,{"derivedFrom":[makeQuery(id+"F6.boolean.opBoolean","COPY",FACE,{"derivedFrom":makeQuery(id+"F6.opExtrude","SWEPT_FACE",FACE,{"disambiguationData":[OSD([sQuery(id+"F4.wireOp",EDGE,"E270.sketch_text.stroke-140")])]})}),makeQuery(id+"F9.opExtrude","SWEPT_FACE",FACE,{"disambiguationData":[OSD([sQuery(id+"F8.wireOp",EDGE,"E533.1")])]})]});
            fillet(context, id + "F13", {"entities" : qUnion([Q0, Q1, Q2, Q3, Q4, Q5, Q6, Q7, Q8, Q9, Q10, Q11, Q12, Q13, Q14, Q15, Q16, Q17, Q18, Q19, Q20, Q21, Q22, Q23]), "radius" : 0.9 * mm, "tangentPropagation" : true, "allowEdgeOverflow" : false});
        }
    });